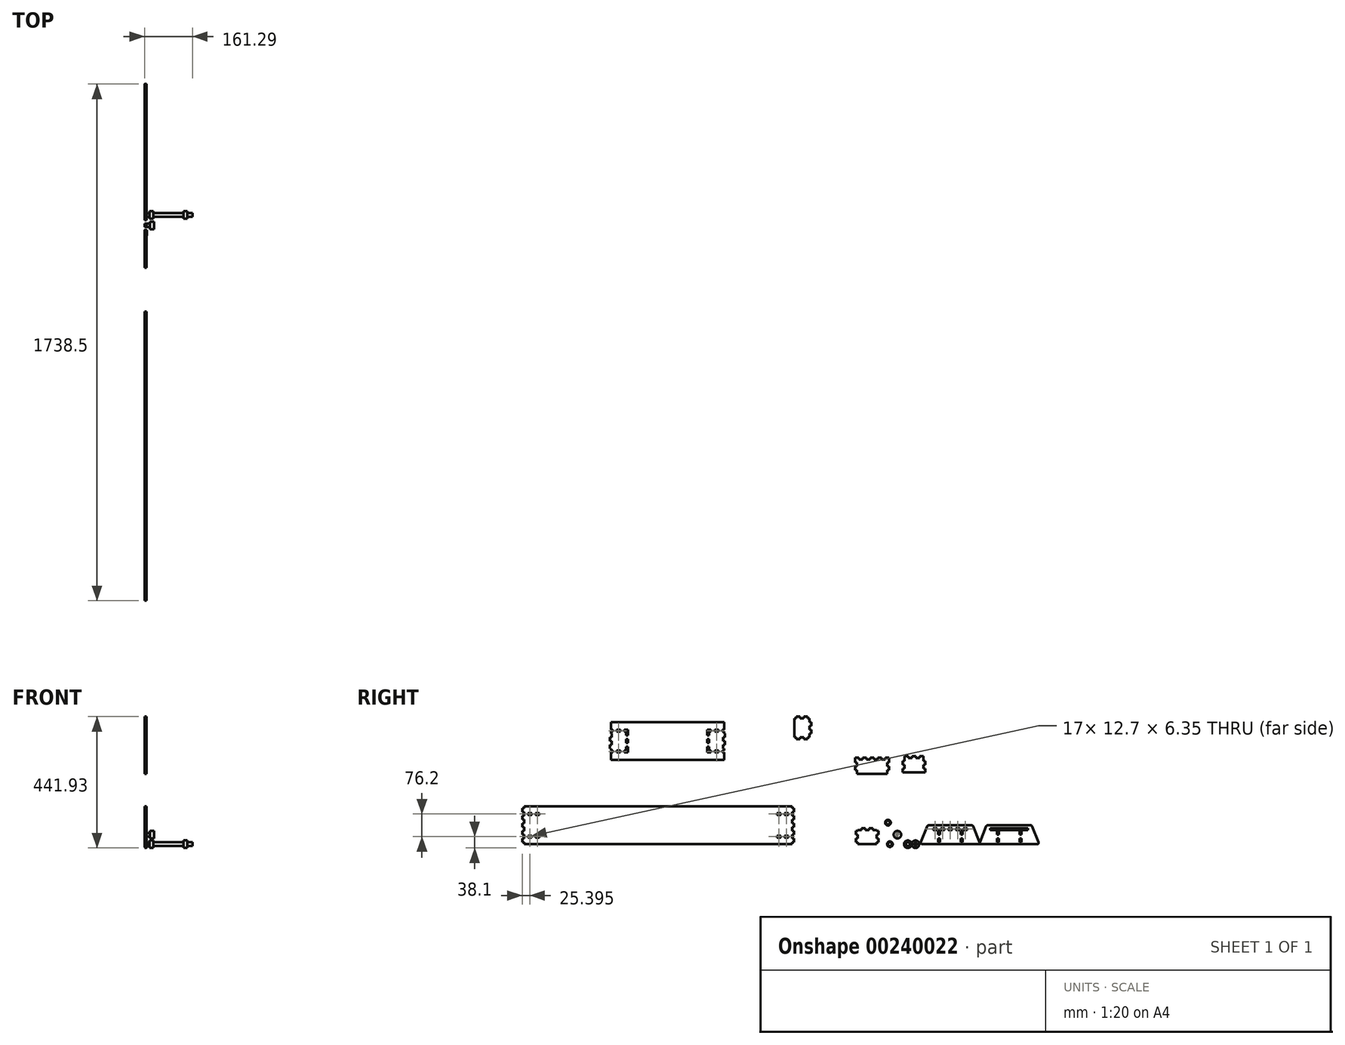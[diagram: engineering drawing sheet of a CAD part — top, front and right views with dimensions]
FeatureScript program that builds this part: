
annotation { "Feature Type Name" : "Feature", "Feature Type Description" : "" }
export const myFeature = defineFeature(function(context is Context, id is Id, definition is map)
    precondition{}
    {
        {
            var Q0;
            Q0=qCreatedBy(makeId("Right.planeOp"),FACE);
            var sketch = newSketch(context, id + "F0", { "sketchPlane" : qUnion([Q0])});
            skLineSegment(sketch, "E0.bottom", {"start": v(0, 0) * mm, "end": v(152.4, 0) * mm});
            skLineSegment(sketch, "E0.top", {"start": v(0, 101.6) * mm, "end": v(152.4, 101.6) * mm});
            skLineSegment(sketch, "E0.left", {"start": v(0, 0) * mm, "end": v(0, 101.6) * mm});
            skLineSegment(sketch, "E0.right", {"start": v(152.4, 0) * mm, "end": v(152.4, 101.6) * mm});
            skLineSegment(sketch, "E1", {"start": v(76.2, 101.6) * mm, "end": v(76.2, 0) * mm, "construction": true});
            skLineSegment(sketch, "E2", {"start": v(0, 50.8) * mm, "end": v(152.4, 50.8) * mm, "construction": true});
            skLineSegment(sketch, "E3", {"start": v(76.2, 53.98) * mm, "end": v(82.55, 53.98) * mm});
            skLineSegment(sketch, "E4", {"start": v(82.55, 53.98) * mm, "end": v(82.55, 50.8) * mm});
            skLineSegment(sketch, "E5.MirrorCS", {"start": v(69.85, 53.98) * mm, "end": v(69.85, 50.8) * mm});
            skLineSegment(sketch, "E6.MirrorCS", {"start": v(76.2, 53.98) * mm, "end": v(69.85, 53.98) * mm});
            skLineSegment(sketch, "E7.MirrorCS", {"start": v(82.55, 47.63) * mm, "end": v(82.55, 50.8) * mm});
            skLineSegment(sketch, "E8.MirrorCS", {"start": v(76.2, 47.63) * mm, "end": v(82.55, 47.63) * mm});
            skLineSegment(sketch, "E9.MirrorCS", {"start": v(76.2, 47.63) * mm, "end": v(69.85, 47.63) * mm});
            skLineSegment(sketch, "E10.MirrorCS", {"start": v(69.85, 47.63) * mm, "end": v(69.85, 50.8) * mm});
            skLineSegment(sketch, "E11.1.0.0", {"start": v(101.6, 53.98) * mm, "end": v(107.95, 53.98) * mm});
            skLineSegment(sketch, "E11.1.0.1", {"start": v(101.6, 53.98) * mm, "end": v(95.25, 53.98) * mm});
            skLineSegment(sketch, "E11.1.0.2", {"start": v(95.25, 53.98) * mm, "end": v(95.25, 50.8) * mm});
            skLineSegment(sketch, "E11.1.0.3", {"start": v(95.25, 47.63) * mm, "end": v(95.25, 50.8) * mm});
            skLineSegment(sketch, "E11.1.0.4", {"start": v(101.6, 47.63) * mm, "end": v(95.25, 47.63) * mm});
            skLineSegment(sketch, "E11.1.0.5", {"start": v(101.6, 47.63) * mm, "end": v(107.95, 47.63) * mm});
            skLineSegment(sketch, "E11.1.0.6", {"start": v(107.95, 47.63) * mm, "end": v(107.95, 50.8) * mm});
            skLineSegment(sketch, "E11.1.0.7", {"start": v(107.95, 53.98) * mm, "end": v(107.95, 50.8) * mm});
            skLineSegment(sketch, "E11.2.0.0", {"start": v(127, 53.98) * mm, "end": v(133.35, 53.98) * mm});
            skLineSegment(sketch, "E11.2.0.1", {"start": v(127, 53.98) * mm, "end": v(120.65, 53.98) * mm});
            skLineSegment(sketch, "E11.2.0.2", {"start": v(120.65, 53.98) * mm, "end": v(120.65, 50.8) * mm});
            skLineSegment(sketch, "E11.2.0.3", {"start": v(120.65, 47.63) * mm, "end": v(120.65, 50.8) * mm});
            skLineSegment(sketch, "E11.2.0.4", {"start": v(127, 47.63) * mm, "end": v(120.65, 47.63) * mm});
            skLineSegment(sketch, "E11.2.0.5", {"start": v(127, 47.63) * mm, "end": v(133.35, 47.63) * mm});
            skLineSegment(sketch, "E11.2.0.6", {"start": v(133.35, 47.63) * mm, "end": v(133.35, 50.8) * mm});
            skLineSegment(sketch, "E11.2.0.7", {"start": v(133.35, 53.98) * mm, "end": v(133.35, 50.8) * mm});
            skLineSegment(sketch, "E11.direction1", {"start": v(76.2, 53.98) * mm, "end": v(101.6, 53.98) * mm, "construction": true});
            skLineSegment(sketch, "E11.direction2", {"start": v(76.2, 53.98) * mm, "end": v(25.4, 53.98) * mm, "construction": true});
            skLineSegment(sketch, "E12.0.0.1", {"start": v(25.4, 53.97) * mm, "end": v(31.75, 53.98) * mm});
            skLineSegment(sketch, "E12.3.0.1", {"start": v(25.4, 53.97) * mm, "end": v(19.05, 53.97) * mm});
            skLineSegment(sketch, "E12.6.0.1", {"start": v(19.05, 53.98) * mm, "end": v(19.05, 50.8) * mm});
            skLineSegment(sketch, "E12.9.0.1", {"start": v(19.05, 47.62) * mm, "end": v(19.05, 50.8) * mm});
            skLineSegment(sketch, "E12.12.0.1", {"start": v(25.4, 47.63) * mm, "end": v(19.05, 47.63) * mm});
            skLineSegment(sketch, "E12.15.0.1", {"start": v(25.4, 47.63) * mm, "end": v(31.75, 47.63) * mm});
            skLineSegment(sketch, "E12.18.0.1", {"start": v(31.75, 47.62) * mm, "end": v(31.75, 50.8) * mm});
            skLineSegment(sketch, "E12.21.0.1", {"start": v(31.75, 53.98) * mm, "end": v(31.75, 50.8) * mm});
            skLineSegment(sketch, "E12.0.1.1", {"start": v(50.8, 53.97) * mm, "end": v(57.15, 53.98) * mm});
            skLineSegment(sketch, "E12.3.1.1", {"start": v(50.8, 53.97) * mm, "end": v(44.45, 53.97) * mm});
            skLineSegment(sketch, "E12.6.1.1", {"start": v(44.45, 53.98) * mm, "end": v(44.45, 50.8) * mm});
            skLineSegment(sketch, "E12.9.1.1", {"start": v(44.45, 47.62) * mm, "end": v(44.45, 50.8) * mm});
            skLineSegment(sketch, "E12.12.1.1", {"start": v(50.8, 47.63) * mm, "end": v(44.45, 47.63) * mm});
            skLineSegment(sketch, "E12.15.1.1", {"start": v(50.8, 47.63) * mm, "end": v(57.15, 47.63) * mm});
            skLineSegment(sketch, "E12.18.1.1", {"start": v(57.15, 47.62) * mm, "end": v(57.15, 50.8) * mm});
            skLineSegment(sketch, "E12.21.1.1", {"start": v(57.15, 53.98) * mm, "end": v(57.15, 50.8) * mm});
            skLineSegment(sketch, "E13.bottom", {"start": v(34.93, 44.45) * mm, "end": v(41.28, 44.45) * mm});
            skLineSegment(sketch, "E13.top", {"start": v(34.93, 31.75) * mm, "end": v(41.28, 31.75) * mm});
            skLineSegment(sketch, "E13.left", {"start": v(34.93, 44.45) * mm, "end": v(34.93, 31.75) * mm});
            skLineSegment(sketch, "E13.right", {"start": v(41.28, 44.45) * mm, "end": v(41.28, 31.75) * mm});
            skLineSegment(sketch, "E14.0.1.0", {"start": v(41.28, 19.05) * mm, "end": v(41.28, 6.35) * mm});
            skLineSegment(sketch, "E14.0.1.1", {"start": v(34.93, 19.05) * mm, "end": v(41.28, 19.05) * mm});
            skLineSegment(sketch, "E14.0.1.2", {"start": v(34.93, 19.05) * mm, "end": v(34.93, 6.35) * mm});
            skLineSegment(sketch, "E14.0.1.3", {"start": v(34.93, 6.35) * mm, "end": v(41.28, 6.35) * mm});
            skLineSegment(sketch, "E14.direction1", {"start": v(41.28, 31.75) * mm, "end": v(53.98, 31.75) * mm, "construction": true});
            skLineSegment(sketch, "E14.direction2", {"start": v(41.28, 31.75) * mm, "end": v(41.28, 6.35) * mm, "construction": true});
            skLineSegment(sketch, "E15.MirrorCS", {"start": v(111.12, 44.45) * mm, "end": v(111.12, 31.75) * mm});
            skLineSegment(sketch, "E16.MirrorCS", {"start": v(117.47, 44.45) * mm, "end": v(111.12, 44.45) * mm});
            skLineSegment(sketch, "E17.MirrorCS", {"start": v(117.47, 44.45) * mm, "end": v(117.47, 31.75) * mm});
            skLineSegment(sketch, "E18.MirrorCS", {"start": v(117.47, 31.75) * mm, "end": v(111.12, 31.75) * mm});
            skLineSegment(sketch, "E19.MirrorCS", {"start": v(117.47, 19.05) * mm, "end": v(111.12, 19.05) * mm});
            skLineSegment(sketch, "E20.MirrorCS", {"start": v(117.47, 19.05) * mm, "end": v(117.47, 6.35) * mm});
            skLineSegment(sketch, "E21.MirrorCS", {"start": v(117.47, 6.35) * mm, "end": v(111.12, 6.35) * mm});
            skLineSegment(sketch, "E22.MirrorCS", {"start": v(111.12, 31.75) * mm, "end": v(111.12, 6.35) * mm, "construction": true});
            skLineSegment(sketch, "E23", {"start": v(111.12, 19.05) * mm, "end": v(111.12, 6.35) * mm});
            skSolve(sketch);
        }
        {
            var Q0;
            Q0=makeQuery(id+"F0.imprint","IMPRINT",FACE,{"disambiguationData":[TD([[makeQuery(id+"F0.imprint","IMPRINT",EDGE,{"derivedFrom":sQuery(id+"F0.wireOp",EDGE,"E0.bottom")}),1.0]])]});
            extrude(context, id + "F1", {"entities" : qUnion([Q0]), "depth" : 6.35 * mm});
        }
        {
            var Q0;
            Q0=qCreatedBy(makeId("Right.planeOp"),FACE);
            var sketch = newSketch(context, id + "F2", { "sketchPlane" : qUnion([Q0])});
            skLineSegment(sketch, "E24.bottom", {"start": v(198.38, 0) * mm, "end": v(350.78, 0) * mm});
            skLineSegment(sketch, "E24.top", {"start": v(198.38, 101.6) * mm, "end": v(350.78, 101.6) * mm});
            skLineSegment(sketch, "E24.left", {"start": v(198.38, 0) * mm, "end": v(198.38, 101.6) * mm});
            skLineSegment(sketch, "E24.right", {"start": v(350.78, 0) * mm, "end": v(350.78, 101.6) * mm});
            skLineSegment(sketch, "E25", {"start": v(198.38, 50.8) * mm, "end": v(350.78, 50.8) * mm, "construction": true});
            skLineSegment(sketch, "E26.bottom", {"start": v(211.08, 53.98) * mm, "end": v(338.08, 53.98) * mm});
            skLineSegment(sketch, "E26.top", {"start": v(211.08, 47.63) * mm, "end": v(338.08, 47.63) * mm});
            skLineSegment(sketch, "E26.left", {"start": v(211.08, 53.98) * mm, "end": v(211.08, 47.63) * mm});
            skLineSegment(sketch, "E26.right", {"start": v(338.08, 53.98) * mm, "end": v(338.08, 47.63) * mm});
            skLineSegment(sketch, "E27.bottom", {"start": v(233.3, 44.45) * mm, "end": v(239.66, 44.45) * mm});
            skLineSegment(sketch, "E27.top", {"start": v(233.3, 31.75) * mm, "end": v(239.66, 31.75) * mm});
            skLineSegment(sketch, "E27.left", {"start": v(233.3, 44.45) * mm, "end": v(233.3, 31.75) * mm});
            skLineSegment(sketch, "E27.right", {"start": v(239.66, 44.45) * mm, "end": v(239.66, 31.75) * mm});
            skLineSegment(sketch, "E28.bottom", {"start": v(233.3, 19.05) * mm, "end": v(239.66, 19.05) * mm});
            skLineSegment(sketch, "E28.top", {"start": v(233.3, 6.35) * mm, "end": v(239.66, 6.35) * mm});
            skLineSegment(sketch, "E28.left", {"start": v(233.3, 19.05) * mm, "end": v(233.3, 6.35) * mm});
            skLineSegment(sketch, "E28.right", {"start": v(239.66, 19.05) * mm, "end": v(239.66, 6.35) * mm});
            skLineSegment(sketch, "E29", {"start": v(274.58, 101.6) * mm, "end": v(274.58, 0) * mm, "construction": true});
            skLineSegment(sketch, "E30.MirrorCS", {"start": v(315.86, 44.45) * mm, "end": v(309.5, 44.45) * mm});
            skLineSegment(sketch, "E31.MirrorCS", {"start": v(315.86, 31.75) * mm, "end": v(309.5, 31.75) * mm});
            skLineSegment(sketch, "E32.MirrorCS", {"start": v(315.86, 44.45) * mm, "end": v(315.86, 31.75) * mm});
            skLineSegment(sketch, "E33.MirrorCS", {"start": v(315.86, 19.05) * mm, "end": v(315.86, 6.35) * mm});
            skLineSegment(sketch, "E34.MirrorCS", {"start": v(315.86, 6.35) * mm, "end": v(309.5, 6.35) * mm});
            skLineSegment(sketch, "E35.MirrorCS", {"start": v(309.5, 19.05) * mm, "end": v(309.5, 6.35) * mm});
            skLineSegment(sketch, "E36.MirrorCS", {"start": v(309.5, 44.45) * mm, "end": v(309.5, 31.75) * mm});
            skLineSegment(sketch, "E37.MirrorCS", {"start": v(315.86, 19.05) * mm, "end": v(309.5, 19.05) * mm});
            skSolve(sketch);
        }
        {
            var Q0;
            Q0=makeQuery(id+"F2.imprint","IMPRINT",FACE,{"disambiguationData":[TD([[makeQuery(id+"F2.imprint","IMPRINT",EDGE,{"derivedFrom":sQuery(id+"F2.wireOp",EDGE,"E24.bottom")}),1.0]])]});
            extrude(context, id + "F3", {"entities" : qUnion([Q0]), "depth" : 6.35 * mm});
        }
        {
            var Q0;
            Q0=qCreatedBy(makeId("Right.planeOp"),FACE);
            var sketch = newSketch(context, id + "F4", { "sketchPlane" : qUnion([Q0])});
            skLineSegment(sketch, "E38.bottom", {"start": v(-164.83, 0) * mm, "end": v(-241.03, 0) * mm});
            skLineSegment(sketch, "E38.top", {"start": v(-164.83, 53.98) * mm, "end": v(-241.03, 53.98) * mm});
            skLineSegment(sketch, "E38.left", {"start": v(-164.83, 0) * mm, "end": v(-164.83, 53.97) * mm});
            skLineSegment(sketch, "E38.right", {"start": v(-241.03, 0) * mm, "end": v(-241.03, 53.98) * mm});
            skLineSegment(sketch, "E39.bottom", {"start": v(-164.83, 0) * mm, "end": v(-171.18, 0) * mm});
            skLineSegment(sketch, "E39.top", {"start": v(-164.83, 6.35) * mm, "end": v(-171.18, 6.35) * mm});
            skLineSegment(sketch, "E39.left", {"start": v(-164.83, 0) * mm, "end": v(-164.83, 6.35) * mm});
            skLineSegment(sketch, "E39.right", {"start": v(-171.18, 0) * mm, "end": v(-171.18, 6.35) * mm});
            skLineSegment(sketch, "E40.bottom", {"start": v(-164.83, 19.05) * mm, "end": v(-171.18, 19.05) * mm});
            skLineSegment(sketch, "E40.top", {"start": v(-164.83, 31.75) * mm, "end": v(-171.18, 31.75) * mm});
            skLineSegment(sketch, "E40.left", {"start": v(-164.83, 19.05) * mm, "end": v(-164.83, 31.75) * mm});
            skLineSegment(sketch, "E40.right", {"start": v(-171.18, 19.05) * mm, "end": v(-171.18, 31.75) * mm});
            skLineSegment(sketch, "E41.bottom", {"start": v(-164.83, 53.98) * mm, "end": v(-171.18, 53.98) * mm});
            skLineSegment(sketch, "E41.top", {"start": v(-164.83, 47.62) * mm, "end": v(-171.18, 47.62) * mm});
            skLineSegment(sketch, "E41.left", {"start": v(-164.83, 53.98) * mm, "end": v(-164.83, 47.62) * mm});
            skLineSegment(sketch, "E42", {"start": v(-202.93, 53.98) * mm, "end": v(-202.93, 0) * mm, "construction": true});
            skLineSegment(sketch, "E43.MirrorCS", {"start": v(-241.03, 47.62) * mm, "end": v(-234.68, 47.62) * mm});
            skLineSegment(sketch, "E44.MirrorCS", {"start": v(-234.68, 53.98) * mm, "end": v(-234.68, 47.62) * mm});
            skLineSegment(sketch, "E45.MirrorCS", {"start": v(-234.68, 19.05) * mm, "end": v(-234.68, 31.75) * mm});
            skLineSegment(sketch, "E46.MirrorCS", {"start": v(-241.03, 31.75) * mm, "end": v(-234.68, 31.75) * mm});
            skLineSegment(sketch, "E47.MirrorCS", {"start": v(-241.03, 19.05) * mm, "end": v(-234.68, 19.05) * mm});
            skLineSegment(sketch, "E48.MirrorCS", {"start": v(-234.68, 0) * mm, "end": v(-234.68, 6.35) * mm});
            skLineSegment(sketch, "E49.MirrorCS", {"start": v(-241.03, 6.35) * mm, "end": v(-234.68, 6.35) * mm});
            skLineSegment(sketch, "E50.bottom", {"start": v(-183.88, 53.98) * mm, "end": v(-196.58, 53.98) * mm});
            skLineSegment(sketch, "E51.bottom", {"start": v(-171.18, 53.98) * mm, "end": v(-183.88, 53.98) * mm});
            skLineSegment(sketch, "E51.top", {"start": v(-171.18, 47.62) * mm, "end": v(-183.88, 47.62) * mm});
            skLineSegment(sketch, "E51.left", {"start": v(-171.18, 53.98) * mm, "end": v(-171.18, 47.62) * mm});
            skLineSegment(sketch, "E51.right", {"start": v(-183.88, 53.98) * mm, "end": v(-183.88, 47.62) * mm});
            skLineSegment(sketch, "E52.MirrorCS", {"start": v(-234.68, 47.62) * mm, "end": v(-221.98, 47.62) * mm});
            skLineSegment(sketch, "E53.MirrorCS", {"start": v(-221.98, 53.98) * mm, "end": v(-221.98, 47.62) * mm});
            skLineSegment(sketch, "E54.bottom", {"start": v(-196.58, 53.98) * mm, "end": v(-202.93, 53.98) * mm});
            skLineSegment(sketch, "E54.top", {"start": v(-196.58, 47.62) * mm, "end": v(-202.93, 47.62) * mm});
            skLineSegment(sketch, "E54.left", {"start": v(-196.58, 53.98) * mm, "end": v(-196.58, 47.62) * mm});
            skLineSegment(sketch, "E54.right", {"start": v(-202.93, 53.98) * mm, "end": v(-202.93, 47.62) * mm});
            skLineSegment(sketch, "E55.MirrorCS", {"start": v(-209.28, 47.62) * mm, "end": v(-202.93, 47.62) * mm});
            skLineSegment(sketch, "E56.MirrorCS", {"start": v(-209.28, 53.98) * mm, "end": v(-209.28, 47.62) * mm});
            skLineSegment(sketch, "E57.top", {"start": v(-164.83, 44.45) * mm, "end": v(-171.18, 44.45) * mm});
            skLineSegment(sketch, "E57.left", {"start": v(-164.83, 47.62) * mm, "end": v(-164.83, 44.45) * mm});
            skLineSegment(sketch, "E57.right", {"start": v(-171.18, 47.62) * mm, "end": v(-171.18, 44.45) * mm});
            skLineSegment(sketch, "E58.MirrorCS", {"start": v(-234.68, 47.62) * mm, "end": v(-234.68, 44.45) * mm});
            skLineSegment(sketch, "E59.MirrorCS", {"start": v(-241.03, 44.45) * mm, "end": v(-234.68, 44.45) * mm});
            skSolve(sketch);
        }
        {
            var Q0;
            {var subQ4=sQuery(id+"F4.wireOp",EDGE,"E39.top");Q0=makeQuery(id+"F4.imprint","IMPRINT",FACE,{"disambiguationData":[TD([[makeQuery(id+"F4.imprint","IMPRINT",EDGE,{"derivedFrom":subQ4}),-1.0]])]});}
            extrude(context, id + "F5", {"entities" : qUnion([Q0]), "depth" : 6.35 * mm});
        }
        {
            var Q0;
            Q0=qCreatedBy(makeId("Right.planeOp"),FACE);
            var sketch = newSketch(context, id + "F6", { "sketchPlane" : qUnion([Q0])});
            skLineSegment(sketch, "E60.bottom", {"start": v(-450.34, 0) * mm, "end": v(-1364.74, 0) * mm});
            skLineSegment(sketch, "E60.top", {"start": v(-450.34, 127) * mm, "end": v(-1364.74, 127) * mm});
            skLineSegment(sketch, "E60.left", {"start": v(-450.34, 0) * mm, "end": v(-450.34, 127) * mm});
            skLineSegment(sketch, "E60.right", {"start": v(-1364.74, 0) * mm, "end": v(-1364.74, 127) * mm});
            skLineSegment(sketch, "E61.bottom", {"start": v(-450.34, 127) * mm, "end": v(-456.7, 127) * mm});
            skLineSegment(sketch, "E61.top", {"start": v(-450.34, 120.65) * mm, "end": v(-456.7, 120.65) * mm});
            skLineSegment(sketch, "E61.left", {"start": v(-450.34, 127) * mm, "end": v(-450.34, 120.65) * mm});
            skLineSegment(sketch, "E61.right", {"start": v(-456.7, 127) * mm, "end": v(-456.7, 120.65) * mm});
            skLineSegment(sketch, "E62.bottom", {"start": v(-450.34, 107.95) * mm, "end": v(-456.7, 107.95) * mm});
            skLineSegment(sketch, "E62.top", {"start": v(-450.34, 95.25) * mm, "end": v(-456.7, 95.25) * mm});
            skLineSegment(sketch, "E62.left", {"start": v(-450.34, 107.95) * mm, "end": v(-450.34, 95.25) * mm});
            skLineSegment(sketch, "E62.right", {"start": v(-456.7, 107.95) * mm, "end": v(-456.7, 95.25) * mm});
            skLineSegment(sketch, "E63.0.1.0", {"start": v(-456.7, 82.55) * mm, "end": v(-456.7, 69.85) * mm});
            skLineSegment(sketch, "E63.0.1.1", {"start": v(-450.34, 69.85) * mm, "end": v(-456.7, 69.85) * mm});
            skLineSegment(sketch, "E63.0.1.2", {"start": v(-450.34, 82.55) * mm, "end": v(-456.7, 82.55) * mm});
            skLineSegment(sketch, "E63.0.2.0", {"start": v(-456.7, 57.15) * mm, "end": v(-456.7, 44.45) * mm});
            skLineSegment(sketch, "E63.0.2.1", {"start": v(-450.34, 44.45) * mm, "end": v(-456.7, 44.45) * mm});
            skLineSegment(sketch, "E63.0.2.2", {"start": v(-450.34, 57.15) * mm, "end": v(-456.7, 57.15) * mm});
            skLineSegment(sketch, "E63.0.3.0", {"start": v(-456.7, 31.75) * mm, "end": v(-456.7, 19.05) * mm});
            skLineSegment(sketch, "E63.0.3.1", {"start": v(-450.34, 19.05) * mm, "end": v(-456.7, 19.05) * mm});
            skLineSegment(sketch, "E63.0.3.2", {"start": v(-450.34, 31.75) * mm, "end": v(-456.7, 31.75) * mm});
            skLineSegment(sketch, "E63.direction1", {"start": v(-456.7, 95.25) * mm, "end": v(-431.3, 95.25) * mm, "construction": true});
            skLineSegment(sketch, "E63.direction2", {"start": v(-456.7, 95.25) * mm, "end": v(-456.7, 69.85) * mm, "construction": true});
            skLineSegment(sketch, "E64", {"start": v(-450.34, 63.5) * mm, "end": v(-1364.74, 63.5) * mm, "construction": true});
            skLineSegment(sketch, "E65.MirrorCS", {"start": v(-450.34, 6.35) * mm, "end": v(-456.7, 6.35) * mm});
            skLineSegment(sketch, "E66.MirrorCS", {"start": v(-456.7, 0) * mm, "end": v(-456.7, 6.35) * mm});
            skLineSegment(sketch, "E67.left", {"start": v(-456.7, 104.78) * mm, "end": v(-456.7, 98.43) * mm});
            skLineSegment(sketch, "E68.direction1", {"start": v(-456.7, 69.85) * mm, "end": v(-482.1, 69.85) * mm, "construction": true});
            skLineSegment(sketch, "E69.MirrorCS", {"start": v(-456.7, 31.75) * mm, "end": v(-456.7, 57.15) * mm, "construction": true});
            skLineSegment(sketch, "E70", {"start": v(-907.54, 0) * mm, "end": v(-907.54, 127) * mm, "construction": true});
            skLineSegment(sketch, "E71.MirrorCS", {"start": v(-1364.74, 127) * mm, "end": v(-1358.4, 127) * mm});
            skLineSegment(sketch, "E72.MirrorCS", {"start": v(-1358.4, 104.77) * mm, "end": v(-1358.4, 98.42) * mm});
            skLineSegment(sketch, "E73.MirrorCS", {"start": v(-1358.4, 82.55) * mm, "end": v(-1358.4, 69.85) * mm});
            skLineSegment(sketch, "E74.MirrorCS", {"start": v(-1364.74, 95.25) * mm, "end": v(-1358.4, 95.25) * mm});
            skLineSegment(sketch, "E75.MirrorCS", {"start": v(-1364.74, 107.95) * mm, "end": v(-1358.4, 107.95) * mm});
            skLineSegment(sketch, "E76.MirrorCS", {"start": v(-1364.74, 120.65) * mm, "end": v(-1358.4, 120.65) * mm});
            skLineSegment(sketch, "E77.MirrorCS", {"start": v(-1358.4, 127) * mm, "end": v(-1358.4, 120.65) * mm});
            skLineSegment(sketch, "E78.MirrorCS", {"start": v(-1364.74, 127) * mm, "end": v(-1364.74, 120.65) * mm});
            skLineSegment(sketch, "E79.MirrorCS", {"start": v(-1364.74, 19.05) * mm, "end": v(-1358.4, 19.05) * mm});
            skLineSegment(sketch, "E80.MirrorCS", {"start": v(-1364.74, 44.45) * mm, "end": v(-1358.4, 44.45) * mm});
            skLineSegment(sketch, "E81.MirrorCS", {"start": v(-1358.4, 107.95) * mm, "end": v(-1358.4, 95.25) * mm});
            skLineSegment(sketch, "E82.MirrorCS", {"start": v(-1364.74, 31.75) * mm, "end": v(-1358.4, 31.75) * mm});
            skLineSegment(sketch, "E83.MirrorCS", {"start": v(-1364.74, 57.15) * mm, "end": v(-1358.4, 57.15) * mm});
            skLineSegment(sketch, "E84.MirrorCS", {"start": v(-1364.74, 6.35) * mm, "end": v(-1358.4, 6.35) * mm});
            skLineSegment(sketch, "E85.MirrorCS", {"start": v(-1364.74, 82.55) * mm, "end": v(-1358.4, 82.55) * mm});
            skLineSegment(sketch, "E86.MirrorCS", {"start": v(-1364.74, 69.85) * mm, "end": v(-1358.4, 69.85) * mm});
            skLineSegment(sketch, "E87.MirrorCS", {"start": v(-1358.4, 95.25) * mm, "end": v(-1358.4, 69.85) * mm, "construction": true});
            skLineSegment(sketch, "E88.MirrorCS", {"start": v(-1358.4, 0) * mm, "end": v(-1358.4, 6.35) * mm});
            skLineSegment(sketch, "E89.MirrorCS", {"start": v(-1358.4, 57.15) * mm, "end": v(-1358.4, 44.45) * mm});
            skLineSegment(sketch, "E90.MirrorCS", {"start": v(-1358.4, 69.85) * mm, "end": v(-1333, 69.85) * mm, "construction": true});
            skLineSegment(sketch, "E91.MirrorCS", {"start": v(-1364.74, 107.95) * mm, "end": v(-1364.74, 95.25) * mm});
            skLineSegment(sketch, "E92.MirrorCS", {"start": v(-1358.4, 31.75) * mm, "end": v(-1358.4, 19.05) * mm});
            skLineSegment(sketch, "E93.MirrorCS", {"start": v(-1364.74, 63.5) * mm, "end": v(-450.34, 63.5) * mm, "construction": true});
            skLineSegment(sketch, "E94.MirrorCS", {"start": v(-1358.4, 31.75) * mm, "end": v(-1358.4, 57.15) * mm, "construction": true});
            skLineSegment(sketch, "E95.MirrorCS", {"start": v(-1358.4, 95.25) * mm, "end": v(-1383.8, 95.25) * mm, "construction": true});
            skLineSegment(sketch, "E96.MirrorCS", {"start": v(-1364.74, 127) * mm, "end": v(-450.34, 127) * mm});
            skLineSegment(sketch, "E97.MirrorCS", {"start": v(-1364.74, 0) * mm, "end": v(-450.34, 0) * mm});
            skLineSegment(sketch, "E98", {"start": v(-456.7, 28.58) * mm, "end": v(-456.7, 22.23) * mm});
            skLineSegment(sketch, "E99", {"start": v(-1358.4, 28.57) * mm, "end": v(-1358.4, 22.22) * mm});
            skLineSegment(sketch, "E100.bottom", {"start": v(-469.4, 104.78) * mm, "end": v(-482.1, 104.78) * mm});
            skLineSegment(sketch, "E100.top", {"start": v(-469.4, 98.43) * mm, "end": v(-482.1, 98.43) * mm});
            skLineSegment(sketch, "E100.left", {"start": v(-469.4, 104.78) * mm, "end": v(-469.4, 98.43) * mm});
            skLineSegment(sketch, "E100.right", {"start": v(-482.1, 104.78) * mm, "end": v(-482.1, 98.43) * mm});
            skLineSegment(sketch, "E101.1.0.0", {"start": v(-494.8, 104.78) * mm, "end": v(-494.8, 98.43) * mm});
            skLineSegment(sketch, "E101.1.0.1", {"start": v(-507.5, 104.78) * mm, "end": v(-507.5, 98.43) * mm});
            skLineSegment(sketch, "E101.1.0.2", {"start": v(-494.8, 98.43) * mm, "end": v(-507.5, 98.43) * mm});
            skLineSegment(sketch, "E101.1.0.3", {"start": v(-494.8, 104.78) * mm, "end": v(-507.5, 104.78) * mm});
            skLineSegment(sketch, "E101.direction1", {"start": v(-482.1, 98.43) * mm, "end": v(-507.5, 98.43) * mm, "construction": true});
            skLineSegment(sketch, "E102.MirrorCS", {"start": v(-494.8, 28.57) * mm, "end": v(-507.5, 28.57) * mm});
            skLineSegment(sketch, "E103.MirrorCS", {"start": v(-507.5, 22.23) * mm, "end": v(-507.5, 28.58) * mm});
            skLineSegment(sketch, "E104.MirrorCS", {"start": v(-482.1, 28.57) * mm, "end": v(-507.5, 28.57) * mm, "construction": true});
            skLineSegment(sketch, "E105.MirrorCS", {"start": v(-482.1, 22.23) * mm, "end": v(-482.1, 28.58) * mm});
            skLineSegment(sketch, "E106.MirrorCS", {"start": v(-469.4, 22.23) * mm, "end": v(-469.4, 28.58) * mm});
            skLineSegment(sketch, "E107.MirrorCS", {"start": v(-469.4, 28.57) * mm, "end": v(-482.1, 28.57) * mm});
            skLineSegment(sketch, "E108.MirrorCS", {"start": v(-469.4, 22.22) * mm, "end": v(-482.1, 22.22) * mm});
            skLineSegment(sketch, "E109.MirrorCS", {"start": v(-494.8, 22.23) * mm, "end": v(-494.8, 28.58) * mm});
            skLineSegment(sketch, "E110.MirrorCS", {"start": v(-494.8, 22.22) * mm, "end": v(-507.5, 22.22) * mm});
            skLineSegment(sketch, "E111.MirrorCS", {"start": v(-1307.6, 104.77) * mm, "end": v(-1307.6, 98.42) * mm});
            skLineSegment(sketch, "E112.MirrorCS", {"start": v(-1320.3, 22.22) * mm, "end": v(-1320.3, 28.57) * mm});
            skLineSegment(sketch, "E113.MirrorCS", {"start": v(-1333, 22.22) * mm, "end": v(-1333, 28.57) * mm});
            skLineSegment(sketch, "E114.MirrorCS", {"start": v(-1307.6, 22.22) * mm, "end": v(-1307.6, 28.57) * mm});
            skLineSegment(sketch, "E115.MirrorCS", {"start": v(-1345.7, 104.77) * mm, "end": v(-1345.7, 98.42) * mm});
            skLineSegment(sketch, "E116.MirrorCS", {"start": v(-1333, 104.77) * mm, "end": v(-1333, 98.42) * mm});
            skLineSegment(sketch, "E117.MirrorCS", {"start": v(-1345.7, 22.22) * mm, "end": v(-1345.7, 28.57) * mm});
            skLineSegment(sketch, "E118.MirrorCS", {"start": v(-1320.3, 104.77) * mm, "end": v(-1320.3, 98.42) * mm});
            skLineSegment(sketch, "E119.MirrorCS", {"start": v(-1320.3, 28.57) * mm, "end": v(-1307.6, 28.57) * mm});
            skLineSegment(sketch, "E120.MirrorCS", {"start": v(-1345.7, 98.43) * mm, "end": v(-1333, 98.43) * mm});
            skLineSegment(sketch, "E121.MirrorCS", {"start": v(-1345.7, 104.78) * mm, "end": v(-1333, 104.78) * mm});
            skLineSegment(sketch, "E122.MirrorCS", {"start": v(-1320.3, 104.78) * mm, "end": v(-1307.6, 104.78) * mm});
            skLineSegment(sketch, "E123.MirrorCS", {"start": v(-1320.3, 98.43) * mm, "end": v(-1307.6, 98.43) * mm});
            skLineSegment(sketch, "E124.MirrorCS", {"start": v(-1333, 28.57) * mm, "end": v(-1307.6, 28.57) * mm, "construction": true});
            skLineSegment(sketch, "E125.MirrorCS", {"start": v(-1345.7, 28.57) * mm, "end": v(-1333, 28.57) * mm});
            skLineSegment(sketch, "E126.MirrorCS", {"start": v(-1320.3, 22.22) * mm, "end": v(-1307.6, 22.22) * mm});
            skLineSegment(sketch, "E127.MirrorCS", {"start": v(-1345.7, 22.22) * mm, "end": v(-1333, 22.22) * mm});
            skLineSegment(sketch, "E128.MirrorCS", {"start": v(-1333, 98.43) * mm, "end": v(-1307.6, 98.43) * mm, "construction": true});
            skSolve(sketch);
        }
        {
            var Q0;
            {var subQ4=sQuery(id+"F6.wireOp",EDGE,"E61.top");Q0=makeQuery(id+"F6.imprint","IMPRINT",FACE,{"disambiguationData":[TD([[makeQuery(id+"F6.imprint","IMPRINT",EDGE,{"derivedFrom":subQ4}),1.0]])]});}
            extrude(context, id + "F7", {"entities" : qUnion([Q0]), "depth" : 6.35 * mm});
        }
        {
            var Q0;
            Q0=qCreatedBy(makeId("Right.planeOp"),FACE);
            var sketch = newSketch(context, id + "F8", { "sketchPlane" : qUnion([Q0])});
            skCircle(sketch, "E129", {"center": v(-101.6, 32.09) * mm, "radius": 5.72 * mm});
            skSolve(sketch);
        }
        {
            var Q0;
            Q0=makeQuery(id+"F8.imprint","IMPRINT",FACE,{"disambiguationData":[TD([[makeQuery(id+"F8.imprint","IMPRINT",EDGE,{"derivedFrom":sQuery(id+"F8.wireOp",EDGE,"E129")}),1.0]])]});
            extrude(context, id + "F9", {"entities" : qUnion([Q0]), "depth" : 19.05 * mm});
        }
        {
            var Q0;
            Q0=qCreatedBy(makeId("Right.planeOp"),FACE);
            var sketch = newSketch(context, id + "F10", { "sketchPlane" : qUnion([Q0])});
            skCircle(sketch, "E130", {"center": v(-66.73, 0) * mm, "radius": 5.72 * mm});
            skSolve(sketch);
        }
        {
            var Q0;
            Q0=makeQuery(id+"F10.imprint","IMPRINT",FACE,{"disambiguationData":[TD([[makeQuery(id+"F10.imprint","IMPRINT",EDGE,{"derivedFrom":sQuery(id+"F10.wireOp",EDGE,"E130")}),1.0]])]});
            extrude(context, id + "F11", {"entities" : qUnion([Q0]), "depth" : 17.14 * mm});
        }
        {
            var Q0;
            Q0=makeQuery(id+"F11.opExtrude","CAP_FACE",FACE,{"disambiguationData":[OSD([sQuery(id+"F10.wireOp",EDGE,"E130")])],"isStart":false});
            var sketch = newSketch(context, id + "F12", { "sketchPlane" : qUnion([Q0])});
            skCircle(sketch, "E131", {"center": v(-66.73, 0) * mm, "radius": 12.7 * mm});
            skSolve(sketch);
        }
        {
            var Q0;
            Q0=makeQuery(id+"F12.imprint","IMPRINT",FACE,{"disambiguationData":[TD([[makeQuery(id+"F12.imprint","IMPRINT",EDGE,{"derivedFrom":sQuery(id+"F12.wireOp",EDGE,"E131")}),1.0]])]});
            var Q1;
            Q1=makeQuery(id+"F12.imprint","IMPRINT",FACE,{"disambiguationData":[TD([[makeQuery(id+"F12.imprint","IMPRINT",EDGE,{"derivedFrom":makeQuery(id+"F11.opExtrude","CAP_EDGE",EDGE,{"disambiguationData":[OSD([sQuery(id+"F10.wireOp",EDGE,"E130")])],"isStart":false})}),1.0]])]});
            extrude(context, id + "F13", {"entities" : qUnion([Q0, Q1]), "operationType" : NewBodyOperationType.ADD, "depth" : 12.7 * mm});
        }
        {
            var Q0;
            Q0=makeQuery(id+"F13.opExtrude","CAP_FACE",FACE,{"disambiguationData":[OSD([sQuery(id+"F12.wireOp",EDGE,"E131")])],"isStart":false});
            var sketch = newSketch(context, id + "F14", { "sketchPlane" : qUnion([Q0])});
            skCircle(sketch, "E132", {"center": v(-66.73, 0) * mm, "radius": 6.35 * mm});
            skSolve(sketch);
        }
        {
            var Q0;
            Q0=makeQuery(id+"F14.imprint","IMPRINT",FACE,{"disambiguationData":[TD([[makeQuery(id+"F14.imprint","IMPRINT",EDGE,{"derivedFrom":sQuery(id+"F14.wireOp",EDGE,"E132")}),1.0]])]});
            extrude(context, id + "F15", {"entities" : qUnion([Q0]), "operationType" : NewBodyOperationType.ADD, "depth" : 101.6 * mm});
        }
        {
            var Q0;
            Q0=makeQuery(id+"F15.opExtrude","CAP_FACE",FACE,{"disambiguationData":[OSD([sQuery(id+"F14.wireOp",EDGE,"E132")])],"isStart":false});
            var sketch = newSketch(context, id + "F16", { "sketchPlane" : qUnion([Q0])});
            skCircle(sketch, "E133", {"center": v(-66.73, 0) * mm, "radius": 12.7 * mm});
            skSolve(sketch);
        }
        {
            var Q0;
            Q0=makeQuery(id+"F16.imprint","IMPRINT",FACE,{"disambiguationData":[TD([[makeQuery(id+"F16.imprint","IMPRINT",EDGE,{"derivedFrom":sQuery(id+"F16.wireOp",EDGE,"E133")}),1.0]])]});
            var Q1;
            Q1=makeQuery(id+"F16.imprint","IMPRINT",FACE,{"disambiguationData":[TD([[makeQuery(id+"F16.imprint","IMPRINT",EDGE,{"derivedFrom":makeQuery(id+"F15.opExtrude","CAP_EDGE",EDGE,{"disambiguationData":[OSD([sQuery(id+"F14.wireOp",EDGE,"E132")])],"isStart":false})}),1.0]])]});
            extrude(context, id + "F17", {"entities" : qUnion([Q0, Q1]), "operationType" : NewBodyOperationType.ADD, "depth" : 12.7 * mm});
        }
        {
            var Q0;
            Q0=makeQuery(id+"F17.opExtrude","CAP_FACE",FACE,{"disambiguationData":[OSD([sQuery(id+"F16.wireOp",EDGE,"E133")])],"isStart":false});
            var sketch = newSketch(context, id + "F18", { "sketchPlane" : qUnion([Q0])});
            skCircle(sketch, "E134", {"center": v(-66.73, 0) * mm, "radius": 6.35 * mm});
            skSolve(sketch);
        }
        {
            var Q0;
            Q0=makeQuery(id+"F18.imprint","IMPRINT",FACE,{"disambiguationData":[TD([[makeQuery(id+"F18.imprint","IMPRINT",EDGE,{"derivedFrom":sQuery(id+"F18.wireOp",EDGE,"E134")}),1.0]])]});
            extrude(context, id + "F19", {"entities" : qUnion([Q0]), "operationType" : NewBodyOperationType.ADD, "depth" : 17.14 * mm});
        }
        {
            var Q0;
            Q0=makeQuery(id+"F9.opExtrude","CAP_FACE",FACE,{"disambiguationData":[OSD([sQuery(id+"F8.wireOp",EDGE,"E129")])],"isStart":false});
            var sketch = newSketch(context, id + "F20", { "sketchPlane" : qUnion([Q0])});
            skCircle(sketch, "E135", {"center": v(-101.6, 32.09) * mm, "radius": 12.7 * mm});
            skSolve(sketch);
        }
        {
            var Q0;
            Q0=makeQuery(id+"F20.imprint","IMPRINT",FACE,{"disambiguationData":[TD([[makeQuery(id+"F20.imprint","IMPRINT",EDGE,{"derivedFrom":sQuery(id+"F20.wireOp",EDGE,"E135")}),1.0]])]});
            var Q1;
            Q1=makeQuery(id+"F20.imprint","IMPRINT",FACE,{"disambiguationData":[TD([[makeQuery(id+"F20.imprint","IMPRINT",EDGE,{"derivedFrom":makeQuery(id+"F9.opExtrude","CAP_EDGE",EDGE,{"disambiguationData":[OSD([sQuery(id+"F8.wireOp",EDGE,"E129")])],"isStart":false})}),1.0]])]});
            extrude(context, id + "F21", {"entities" : qUnion([Q0, Q1]), "operationType" : NewBodyOperationType.ADD, "depth" : 12.7 * mm});
        }
        {
            var Q0;
            Q0=qCreatedBy(makeId("Top.planeOp"),FACE);
            var sketch = newSketch(context, id + "F22", { "sketchPlane" : qUnion([Q0])});
            skCircle(sketch, "E136", {"center": v(4.76, -101.6) * mm, "radius": 1.59 * mm});
            skSolve(sketch);
        }
        {
            var Q0;
            Q0=qSketchRegion(id+"F22",true);
            extrude(context, id + "F23", {"entities" : qUnion([Q0]), "operationType" : NewBodyOperationType.REMOVE, "endBound" : BoundingType.THROUGH_ALL, "depth" : 25.4 * mm});
        }
        {
            var Q0;
            Q0=qCreatedBy(makeId("Right.planeOp"),FACE);
            var sketch = newSketch(context, id + "F24", { "sketchPlane" : qUnion([Q0])});
            skCircle(sketch, "E137", {"center": v(-127, 0) * mm, "radius": 9.53 * mm});
            skSolve(sketch);
        }
        {
            var Q0;
            Q0=makeQuery(id+"F24.imprint","IMPRINT",FACE,{"disambiguationData":[TD([[makeQuery(id+"F24.imprint","IMPRINT",EDGE,{"derivedFrom":sQuery(id+"F24.wireOp",EDGE,"E137")}),1.0]])]});
            extrude(context, id + "F25", {"entities" : qUnion([Q0]), "depth" : 8.47 * mm});
        }
        {
            var Q0;
            Q0=qCreatedBy(makeId("Top.planeOp"),FACE);
            var sketch = newSketch(context, id + "F26", { "sketchPlane" : qUnion([Q0])});
            skCircle(sketch, "E138", {"center": v(4.23, -127) * mm, "radius": 1.59 * mm});
            skSolve(sketch);
        }
        {
            var Q0;
            Q0=qSketchRegion(id+"F26",true);
            extrude(context, id + "F27", {"entities" : qUnion([Q0]), "operationType" : NewBodyOperationType.REMOVE, "endBound" : BoundingType.THROUGH_ALL, "depth" : 25.4 * mm});
        }
        {
            var Q0;
            Q0=makeQuery(id+"F25.opExtrude","CAP_FACE",FACE,{"disambiguationData":[OSD([sQuery(id+"F24.wireOp",EDGE,"E137")])],"isStart":true});
            var sketch = newSketch(context, id + "F28", { "sketchPlane" : qUnion([Q0])});
            skCircle(sketch, "E139", {"center": v(127, 0) * mm, "radius": 6.35 * mm});
            skSolve(sketch);
        }
        {
            var Q0;
            Q0=makeQuery(id+"F28.imprint","IMPRINT",FACE,{"disambiguationData":[TD([[makeQuery(id+"F28.imprint","IMPRINT",EDGE,{"derivedFrom":sQuery(id+"F28.wireOp",EDGE,"E139")}),1.0]])]});
            extrude(context, id + "F29", {"entities" : qUnion([Q0]), "operationType" : NewBodyOperationType.REMOVE, "endBound" : BoundingType.UP_TO_NEXT, "oppositeDirection" : true, "depth" : 25.4 * mm});
        }
        {
            var Q0;
            Q0=qCreatedBy(makeId("Right.planeOp"),FACE);
            var sketch = newSketch(context, id + "F30", { "sketchPlane" : qUnion([Q0])});
            skCircle(sketch, "E140", {"center": v(-133.45, 72.65) * mm, "radius": 9.53 * mm});
            skCircle(sketch, "E141", {"center": v(-133.45, 72.65) * mm, "radius": 6.35 * mm});
            skSolve(sketch);
        }
        {
            var Q0;
            Q0=makeQuery(id+"F30.imprint","IMPRINT",FACE,{"disambiguationData":[TD([[makeQuery(id+"F30.imprint","IMPRINT",EDGE,{"derivedFrom":sQuery(id+"F30.wireOp",EDGE,"E140")}),1.0]])]});
            extrude(context, id + "F31", {"entities" : qUnion([Q0]), "depth" : 2.38 * mm});
        }
        {
            var Q0;
            Q0=makeQuery(id+"F5.opExtrude","SWEPT_BODY",BODY,{"disambiguationData":[OSD([sQuery(id+"F4.wireOp",EDGE,"E38.bottom"),sQuery(id+"F4.wireOp",EDGE,"E38.top"),sQuery(id+"F4.wireOp",EDGE,"E38.left"),sQuery(id+"F4.wireOp",EDGE,"E38.right"),sQuery(id+"F4.wireOp",EDGE,"E39.top"),sQuery(id+"F4.wireOp",EDGE,"E39.right"),sQuery(id+"F4.wireOp",EDGE,"E40.bottom"),sQuery(id+"F4.wireOp",EDGE,"E40.top"),sQuery(id+"F4.wireOp",EDGE,"E40.right"),sQuery(id+"F4.wireOp",EDGE,"E45.MirrorCS"),sQuery(id+"F4.wireOp",EDGE,"E46.MirrorCS"),sQuery(id+"F4.wireOp",EDGE,"E47.MirrorCS"),sQuery(id+"F4.wireOp",EDGE,"E48.MirrorCS"),sQuery(id+"F4.wireOp",EDGE,"E49.MirrorCS"),sQuery(id+"F4.wireOp",EDGE,"E50.bottom"),sQuery(id+"F4.wireOp",EDGE,"E51.top"),sQuery(id+"F4.wireOp",EDGE,"E51.right"),sQuery(id+"F4.wireOp",EDGE,"E52.MirrorCS"),sQuery(id+"F4.wireOp",EDGE,"E53.MirrorCS"),sQuery(id+"F4.wireOp",EDGE,"E54.top"),sQuery(id+"F4.wireOp",EDGE,"E54.left"),sQuery(id+"F4.wireOp",EDGE,"E55.MirrorCS"),sQuery(id+"F4.wireOp",EDGE,"E56.MirrorCS"),sQuery(id+"F4.wireOp",EDGE,"E57.top"),sQuery(id+"F4.wireOp",EDGE,"E57.right"),sQuery(id+"F4.wireOp",EDGE,"E58.MirrorCS"),sQuery(id+"F4.wireOp",EDGE,"E59.MirrorCS")])]});
            transform(context, id + "F32", {"entities" : qUnion([Q0]), "transformType" : TransformType.TRANSLATION_3D, "dx" : 0 * mm, "dy" : 0 * mm, "dz" : 0 * mm, "makeCopy" : true});
        }
        {
            var Q0;
            Q0=makeQuery(id+"F32.opPattern","COPY",BODY,{"derivedFrom":makeQuery(id+"F5.opExtrude","SWEPT_BODY",BODY,{"disambiguationData":[OSD([sQuery(id+"F4.wireOp",EDGE,"E38.bottom"),sQuery(id+"F4.wireOp",EDGE,"E38.top"),sQuery(id+"F4.wireOp",EDGE,"E38.left"),sQuery(id+"F4.wireOp",EDGE,"E38.right"),sQuery(id+"F4.wireOp",EDGE,"E39.top"),sQuery(id+"F4.wireOp",EDGE,"E39.right"),sQuery(id+"F4.wireOp",EDGE,"E40.bottom"),sQuery(id+"F4.wireOp",EDGE,"E40.top"),sQuery(id+"F4.wireOp",EDGE,"E40.right"),sQuery(id+"F4.wireOp",EDGE,"E45.MirrorCS"),sQuery(id+"F4.wireOp",EDGE,"E46.MirrorCS"),sQuery(id+"F4.wireOp",EDGE,"E47.MirrorCS"),sQuery(id+"F4.wireOp",EDGE,"E48.MirrorCS"),sQuery(id+"F4.wireOp",EDGE,"E49.MirrorCS"),sQuery(id+"F4.wireOp",EDGE,"E50.bottom"),sQuery(id+"F4.wireOp",EDGE,"E51.top"),sQuery(id+"F4.wireOp",EDGE,"E51.right"),sQuery(id+"F4.wireOp",EDGE,"E52.MirrorCS"),sQuery(id+"F4.wireOp",EDGE,"E53.MirrorCS"),sQuery(id+"F4.wireOp",EDGE,"E54.top"),sQuery(id+"F4.wireOp",EDGE,"E54.left"),sQuery(id+"F4.wireOp",EDGE,"E55.MirrorCS"),sQuery(id+"F4.wireOp",EDGE,"E56.MirrorCS"),sQuery(id+"F4.wireOp",EDGE,"E57.top"),sQuery(id+"F4.wireOp",EDGE,"E57.right"),sQuery(id+"F4.wireOp",EDGE,"E58.MirrorCS"),sQuery(id+"F4.wireOp",EDGE,"E59.MirrorCS")])]}),"instanceName":"1"});
            deleteBodies(context, id + "F33", {"entities" : qUnion([Q0])});
        }
        {
            var Q0;
            Q0=qCreatedBy(makeId("Right.planeOp"),FACE);
            var sketch = newSketch(context, id + "F34", { "sketchPlane" : qUnion([Q0])});
            skLineSegment(sketch, "E142.bottom", {"start": v(-244.06, 237.28) * mm, "end": v(-129.76, 237.28) * mm});
            skLineSegment(sketch, "E142.top", {"start": v(-244.06, 291.25) * mm, "end": v(-129.76, 291.25) * mm});
            skLineSegment(sketch, "E142.left", {"start": v(-244.06, 237.28) * mm, "end": v(-244.06, 291.25) * mm});
            skLineSegment(sketch, "E142.right", {"start": v(-129.76, 237.28) * mm, "end": v(-129.76, 291.25) * mm});
            skLineSegment(sketch, "E143.bottom", {"start": v(-244.06, 237.28) * mm, "end": v(-237.71, 237.28) * mm});
            skLineSegment(sketch, "E143.top", {"start": v(-244.06, 249.98) * mm, "end": v(-237.71, 249.98) * mm});
            skLineSegment(sketch, "E143.left", {"start": v(-244.06, 237.28) * mm, "end": v(-244.06, 249.98) * mm});
            skLineSegment(sketch, "E143.right", {"start": v(-237.71, 237.28) * mm, "end": v(-237.71, 249.98) * mm});
            skLineSegment(sketch, "E144.bottom", {"start": v(-244.06, 275.38) * mm, "end": v(-237.71, 275.38) * mm});
            skLineSegment(sketch, "E144.top", {"start": v(-244.06, 262.68) * mm, "end": v(-237.71, 262.68) * mm});
            skLineSegment(sketch, "E144.left", {"start": v(-244.06, 275.38) * mm, "end": v(-244.06, 262.68) * mm});
            skLineSegment(sketch, "E144.right", {"start": v(-237.71, 275.38) * mm, "end": v(-237.71, 262.68) * mm});
            skLineSegment(sketch, "E145.bottom", {"start": v(-231.36, 291.25) * mm, "end": v(-218.66, 291.25) * mm});
            skLineSegment(sketch, "E145.top", {"start": v(-231.36, 284.9) * mm, "end": v(-218.66, 284.9) * mm});
            skLineSegment(sketch, "E145.left", {"start": v(-231.36, 291.25) * mm, "end": v(-231.36, 284.9) * mm});
            skLineSegment(sketch, "E145.right", {"start": v(-218.66, 291.25) * mm, "end": v(-218.66, 284.9) * mm});
            skLineSegment(sketch, "E146.1.0.0", {"start": v(-205.96, 291.25) * mm, "end": v(-205.96, 284.9) * mm});
            skLineSegment(sketch, "E146.1.0.1", {"start": v(-193.26, 291.25) * mm, "end": v(-193.26, 284.9) * mm});
            skLineSegment(sketch, "E146.1.0.2", {"start": v(-205.96, 291.25) * mm, "end": v(-193.26, 291.25) * mm});
            skLineSegment(sketch, "E146.1.0.3", {"start": v(-205.96, 284.9) * mm, "end": v(-193.26, 284.9) * mm});
            skLineSegment(sketch, "E146.2.0.0", {"start": v(-180.56, 291.25) * mm, "end": v(-180.56, 284.9) * mm});
            skLineSegment(sketch, "E146.2.0.1", {"start": v(-167.86, 291.25) * mm, "end": v(-167.86, 284.9) * mm});
            skLineSegment(sketch, "E146.2.0.2", {"start": v(-180.56, 291.25) * mm, "end": v(-167.86, 291.25) * mm});
            skLineSegment(sketch, "E146.2.0.3", {"start": v(-180.56, 284.9) * mm, "end": v(-167.86, 284.9) * mm});
            skLineSegment(sketch, "E146.3.0.0", {"start": v(-155.16, 291.25) * mm, "end": v(-155.16, 284.9) * mm});
            skLineSegment(sketch, "E146.3.0.1", {"start": v(-142.46, 291.25) * mm, "end": v(-142.46, 284.9) * mm});
            skLineSegment(sketch, "E146.3.0.2", {"start": v(-155.16, 291.25) * mm, "end": v(-142.46, 291.25) * mm});
            skLineSegment(sketch, "E146.3.0.3", {"start": v(-155.16, 284.9) * mm, "end": v(-142.46, 284.9) * mm});
            skLineSegment(sketch, "E146.direction1", {"start": v(-244.06, 291.25) * mm, "end": v(-218.66, 291.25) * mm, "construction": true});
            skLineSegment(sketch, "E147", {"start": v(-186.91, 291.25) * mm, "end": v(-186.91, 237.28) * mm, "construction": true});
            skLineSegment(sketch, "E148.MirrorCS", {"start": v(-129.76, 262.68) * mm, "end": v(-136.11, 262.68) * mm});
            skLineSegment(sketch, "E149.MirrorCS", {"start": v(-129.76, 275.38) * mm, "end": v(-136.11, 275.38) * mm});
            skLineSegment(sketch, "E150.MirrorCS", {"start": v(-136.11, 275.38) * mm, "end": v(-136.11, 262.68) * mm});
            skLineSegment(sketch, "E151.MirrorCS", {"start": v(-129.76, 249.98) * mm, "end": v(-136.11, 249.98) * mm});
            skLineSegment(sketch, "E152.MirrorCS", {"start": v(-136.11, 237.28) * mm, "end": v(-136.11, 249.98) * mm});
            skSolve(sketch);
        }
        {
            var Q0;
            {var subQ6=sQuery(id+"F34.wireOp",EDGE,"E143.top");Q0=makeQuery(id+"F34.imprint","IMPRINT",FACE,{"disambiguationData":[TD([[makeQuery(id+"F34.imprint","IMPRINT",EDGE,{"derivedFrom":subQ6}),1.0]])]});}
            extrude(context, id + "F35", {"entities" : qUnion([Q0]), "depth" : 6.35 * mm});
        }
        {
            var Q0;
            Q0=qCreatedBy(makeId("Right.planeOp"),FACE);
            var sketch = newSketch(context, id + "F36", { "sketchPlane" : qUnion([Q0])});
            skLineSegment(sketch, "E153.bottom", {"start": v(-83.94, 241.82) * mm, "end": v(-7.74, 241.82) * mm});
            skLineSegment(sketch, "E153.top", {"start": v(-83.94, 295.8) * mm, "end": v(-7.74, 295.8) * mm});
            skLineSegment(sketch, "E153.left", {"start": v(-83.94, 241.82) * mm, "end": v(-83.94, 295.8) * mm});
            skLineSegment(sketch, "E153.right", {"start": v(-7.74, 241.82) * mm, "end": v(-7.74, 295.8) * mm});
            skLineSegment(sketch, "E154.bottom", {"start": v(-83.94, 295.8) * mm, "end": v(-77.59, 295.8) * mm});
            skLineSegment(sketch, "E154.top", {"start": v(-83.94, 279.92) * mm, "end": v(-77.59, 279.92) * mm});
            skLineSegment(sketch, "E154.left", {"start": v(-83.94, 295.8) * mm, "end": v(-83.94, 279.92) * mm});
            skLineSegment(sketch, "E154.right", {"start": v(-77.59, 295.8) * mm, "end": v(-77.59, 279.92) * mm});
            skLineSegment(sketch, "E155.bottom", {"start": v(-83.94, 254.52) * mm, "end": v(-77.59, 254.52) * mm});
            skLineSegment(sketch, "E155.top", {"start": v(-83.94, 267.22) * mm, "end": v(-77.59, 267.22) * mm});
            skLineSegment(sketch, "E155.left", {"start": v(-83.94, 254.52) * mm, "end": v(-83.94, 267.22) * mm});
            skLineSegment(sketch, "E155.right", {"start": v(-77.59, 254.52) * mm, "end": v(-77.59, 267.22) * mm});
            skLineSegment(sketch, "E156.bottom", {"start": v(-64.89, 295.8) * mm, "end": v(-52.19, 295.8) * mm});
            skLineSegment(sketch, "E156.top", {"start": v(-64.89, 289.44) * mm, "end": v(-52.19, 289.44) * mm});
            skLineSegment(sketch, "E156.left", {"start": v(-64.89, 295.8) * mm, "end": v(-64.89, 289.44) * mm});
            skLineSegment(sketch, "E156.right", {"start": v(-52.19, 295.8) * mm, "end": v(-52.19, 289.44) * mm});
            skLineSegment(sketch, "E157.1.0.0", {"start": v(-26.79, 295.8) * mm, "end": v(-26.79, 289.44) * mm});
            skLineSegment(sketch, "E157.1.0.1", {"start": v(-39.49, 289.44) * mm, "end": v(-26.79, 289.44) * mm});
            skLineSegment(sketch, "E157.1.0.2", {"start": v(-39.49, 295.8) * mm, "end": v(-39.49, 289.44) * mm});
            skLineSegment(sketch, "E157.direction1", {"start": v(-64.89, 289.44) * mm, "end": v(-39.49, 289.44) * mm, "construction": true});
            skLineSegment(sketch, "E158", {"start": v(-45.84, 241.82) * mm, "end": v(-45.84, 295.8) * mm, "construction": true});
            skLineSegment(sketch, "E159.MirrorCS", {"start": v(-7.74, 254.52) * mm, "end": v(-14.09, 254.52) * mm});
            skLineSegment(sketch, "E160.MirrorCS", {"start": v(-7.74, 267.22) * mm, "end": v(-14.09, 267.22) * mm});
            skLineSegment(sketch, "E161.MirrorCS", {"start": v(-7.74, 279.92) * mm, "end": v(-14.09, 279.92) * mm});
            skLineSegment(sketch, "E162.MirrorCS", {"start": v(-14.09, 295.8) * mm, "end": v(-14.09, 279.92) * mm});
            skLineSegment(sketch, "E163.MirrorCS", {"start": v(-14.09, 254.52) * mm, "end": v(-14.09, 267.22) * mm});
            skSolve(sketch);
        }
        {
            var Q0;
            {var subQ13=sQuery(id+"F36.wireOp",EDGE,"E153.bottom");Q0=makeQuery(id+"F36.imprint","IMPRINT",FACE,{"disambiguationData":[TD([[makeQuery(id+"F36.imprint","IMPRINT",EDGE,{"derivedFrom":subQ13}),1.0]])]});}
            extrude(context, id + "F37", {"entities" : qUnion([Q0]), "depth" : 6.35 * mm});
        }
        {
            var Q0;
            Q0=qCreatedBy(makeId("Right.planeOp"),FACE);
            var sketch = newSketch(context, id + "F38", { "sketchPlane" : qUnion([Q0])});
            skLineSegment(sketch, "E164.bottom", {"start": v(-505.29, 353.03) * mm, "end": v(-390.99, 353.03) * mm});
            skLineSegment(sketch, "E164.top", {"start": v(-505.29, 429.23) * mm, "end": v(-390.99, 429.23) * mm});
            skLineSegment(sketch, "E164.left", {"start": v(-505.29, 353.03) * mm, "end": v(-505.29, 429.23) * mm});
            skLineSegment(sketch, "E164.right", {"start": v(-390.99, 353.03) * mm, "end": v(-390.99, 429.23) * mm});
            skLineSegment(sketch, "E165.bottom", {"start": v(-505.29, 429.23) * mm, "end": v(-492.59, 429.23) * mm});
            skLineSegment(sketch, "E165.top", {"start": v(-505.29, 422.88) * mm, "end": v(-492.59, 422.88) * mm});
            skLineSegment(sketch, "E165.left", {"start": v(-505.29, 429.23) * mm, "end": v(-505.29, 422.88) * mm});
            skLineSegment(sketch, "E165.right", {"start": v(-492.59, 429.23) * mm, "end": v(-492.59, 422.88) * mm});
            skLineSegment(sketch, "E166", {"start": v(-448.14, 429.23) * mm, "end": v(-448.14, 353.03) * mm, "construction": true});
            skLineSegment(sketch, "E167.1.0.0", {"start": v(-467.19, 429.23) * mm, "end": v(-467.19, 422.88) * mm});
            skLineSegment(sketch, "E167.1.0.1", {"start": v(-479.89, 422.88) * mm, "end": v(-467.19, 422.88) * mm});
            skLineSegment(sketch, "E167.1.0.2", {"start": v(-479.89, 429.23) * mm, "end": v(-467.19, 429.23) * mm});
            skLineSegment(sketch, "E167.1.0.3", {"start": v(-479.89, 429.23) * mm, "end": v(-479.89, 422.88) * mm});
            skLineSegment(sketch, "E167.2.0.0", {"start": v(-441.79, 429.23) * mm, "end": v(-441.79, 422.88) * mm});
            skLineSegment(sketch, "E167.2.0.1", {"start": v(-454.49, 422.88) * mm, "end": v(-441.79, 422.88) * mm});
            skLineSegment(sketch, "E167.2.0.2", {"start": v(-454.49, 429.23) * mm, "end": v(-441.79, 429.23) * mm});
            skLineSegment(sketch, "E167.2.0.3", {"start": v(-454.49, 429.23) * mm, "end": v(-454.49, 422.88) * mm});
            skLineSegment(sketch, "E167.3.0.0", {"start": v(-416.39, 429.23) * mm, "end": v(-416.39, 422.88) * mm});
            skLineSegment(sketch, "E167.3.0.1", {"start": v(-429.09, 422.88) * mm, "end": v(-416.39, 422.88) * mm});
            skLineSegment(sketch, "E167.3.0.2", {"start": v(-429.09, 429.23) * mm, "end": v(-416.39, 429.23) * mm});
            skLineSegment(sketch, "E167.3.0.3", {"start": v(-429.09, 429.23) * mm, "end": v(-429.09, 422.88) * mm});
            skLineSegment(sketch, "E167.4.0.0", {"start": v(-390.99, 429.23) * mm, "end": v(-390.99, 422.88) * mm});
            skLineSegment(sketch, "E167.4.0.1", {"start": v(-403.69, 422.88) * mm, "end": v(-390.99, 422.88) * mm});
            skLineSegment(sketch, "E167.4.0.2", {"start": v(-403.69, 429.23) * mm, "end": v(-390.99, 429.23) * mm});
            skLineSegment(sketch, "E167.4.0.3", {"start": v(-403.69, 429.23) * mm, "end": v(-403.69, 422.88) * mm});
            skLineSegment(sketch, "E167.direction1", {"start": v(-505.29, 422.88) * mm, "end": v(-479.89, 422.88) * mm, "construction": true});
            skPoint(sketch, "E168.oppositeSnap0", {"position": v(-498.94, 422.88) * mm});
            skLineSegment(sketch, "E168.bottom", {"start": v(-505.29, 359.38) * mm, "end": v(-498.94, 359.38) * mm});
            skLineSegment(sketch, "E168.top", {"start": v(-505.29, 372.08) * mm, "end": v(-498.94, 372.08) * mm});
            skLineSegment(sketch, "E168.left", {"start": v(-505.29, 359.38) * mm, "end": v(-505.29, 372.08) * mm});
            skLineSegment(sketch, "E168.right", {"start": v(-498.94, 359.38) * mm, "end": v(-498.94, 372.08) * mm});
            skLineSegment(sketch, "E169.0.1.0", {"start": v(-498.94, 384.78) * mm, "end": v(-498.94, 397.48) * mm});
            skLineSegment(sketch, "E169.0.1.1", {"start": v(-505.29, 384.78) * mm, "end": v(-498.94, 384.78) * mm});
            skLineSegment(sketch, "E169.0.1.2", {"start": v(-505.29, 397.48) * mm, "end": v(-498.94, 397.48) * mm});
            skLineSegment(sketch, "E169.0.1.3", {"start": v(-505.29, 384.78) * mm, "end": v(-505.29, 397.48) * mm});
            skLineSegment(sketch, "E169.0.2.0", {"start": v(-498.94, 410.18) * mm, "end": v(-498.94, 422.88) * mm});
            skLineSegment(sketch, "E169.0.2.1", {"start": v(-505.29, 410.18) * mm, "end": v(-498.94, 410.18) * mm});
            skLineSegment(sketch, "E169.0.2.2", {"start": v(-505.29, 422.88) * mm, "end": v(-498.94, 422.88) * mm});
            skLineSegment(sketch, "E169.0.2.3", {"start": v(-505.29, 410.18) * mm, "end": v(-505.29, 422.88) * mm});
            skLineSegment(sketch, "E169.direction1", {"start": v(-505.29, 359.38) * mm, "end": v(-479.89, 359.38) * mm, "construction": true});
            skLineSegment(sketch, "E169.direction2", {"start": v(-505.29, 359.38) * mm, "end": v(-505.29, 384.78) * mm, "construction": true});
            skLineSegment(sketch, "E170", {"start": v(-505.29, 391.13) * mm, "end": v(-390.99, 391.13) * mm, "construction": true});
            skLineSegment(sketch, "E171.MirrorCS", {"start": v(-505.29, 359.38) * mm, "end": v(-492.59, 359.38) * mm});
            skLineSegment(sketch, "E172.MirrorCS", {"start": v(-479.89, 359.38) * mm, "end": v(-467.19, 359.38) * mm});
            skLineSegment(sketch, "E173.MirrorCS", {"start": v(-467.19, 353.03) * mm, "end": v(-467.19, 359.38) * mm});
            skLineSegment(sketch, "E174.MirrorCS", {"start": v(-479.89, 353.03) * mm, "end": v(-479.89, 359.38) * mm});
            skLineSegment(sketch, "E175.MirrorCS", {"start": v(-429.09, 359.38) * mm, "end": v(-416.39, 359.38) * mm});
            skLineSegment(sketch, "E176.MirrorCS", {"start": v(-492.59, 353.03) * mm, "end": v(-492.59, 359.38) * mm});
            skLineSegment(sketch, "E177.MirrorCS", {"start": v(-403.69, 359.38) * mm, "end": v(-390.99, 359.38) * mm});
            skLineSegment(sketch, "E178.MirrorCS", {"start": v(-416.39, 353.03) * mm, "end": v(-416.39, 359.38) * mm});
            skLineSegment(sketch, "E179.MirrorCS", {"start": v(-441.79, 353.03) * mm, "end": v(-441.79, 359.38) * mm});
            skLineSegment(sketch, "E180.MirrorCS", {"start": v(-429.09, 353.03) * mm, "end": v(-429.09, 359.38) * mm});
            skLineSegment(sketch, "E181.MirrorCS", {"start": v(-454.49, 359.38) * mm, "end": v(-441.79, 359.38) * mm});
            skLineSegment(sketch, "E182.MirrorCS", {"start": v(-448.14, 353.03) * mm, "end": v(-448.14, 429.23) * mm, "construction": true});
            skLineSegment(sketch, "E183.MirrorCS", {"start": v(-403.69, 353.03) * mm, "end": v(-403.69, 359.38) * mm});
            skLineSegment(sketch, "E184.MirrorCS", {"start": v(-454.49, 353.03) * mm, "end": v(-454.49, 359.38) * mm});
            skLineSegment(sketch, "E185.MirrorCS", {"start": v(-390.99, 384.78) * mm, "end": v(-397.34, 384.78) * mm});
            skLineSegment(sketch, "E186.MirrorCS", {"start": v(-397.34, 359.38) * mm, "end": v(-397.34, 372.08) * mm});
            skLineSegment(sketch, "E187.MirrorCS", {"start": v(-390.99, 397.48) * mm, "end": v(-397.34, 397.48) * mm});
            skLineSegment(sketch, "E188.MirrorCS", {"start": v(-390.99, 391.13) * mm, "end": v(-505.29, 391.13) * mm, "construction": true});
            skLineSegment(sketch, "E189.MirrorCS", {"start": v(-397.34, 384.78) * mm, "end": v(-397.34, 397.48) * mm});
            skLineSegment(sketch, "E190.MirrorCS", {"start": v(-390.99, 410.18) * mm, "end": v(-397.34, 410.18) * mm});
            skLineSegment(sketch, "E191.MirrorCS", {"start": v(-397.34, 410.18) * mm, "end": v(-397.34, 422.88) * mm});
            skLineSegment(sketch, "E192.MirrorCS", {"start": v(-390.99, 372.08) * mm, "end": v(-397.34, 372.08) * mm});
            skPoint(sketch, "E193.firstSnap0", {"position": v(-448.14, 359.38) * mm});
            skLineSegment(sketch, "E193.bottom", {"start": v(-448.14, 327.63) * mm, "end": v(-143.34, 327.63) * mm});
            skLineSegment(sketch, "E193.top", {"start": v(-448.14, 454.63) * mm, "end": v(-143.34, 454.63) * mm});
            skLineSegment(sketch, "E193.left", {"start": v(-448.14, 327.63) * mm, "end": v(-448.14, 454.63) * mm});
            skLineSegment(sketch, "E193.right", {"start": v(-143.34, 327.63) * mm, "end": v(-143.34, 454.63) * mm});
            skLineSegment(sketch, "E194", {"start": v(-295.74, 454.63) * mm, "end": v(-295.74, 327.63) * mm, "construction": true});
            skLineSegment(sketch, "E195.MirrorCS", {"start": v(-149.69, 429.23) * mm, "end": v(-149.69, 422.88) * mm});
            skLineSegment(sketch, "E196.MirrorCS", {"start": v(-187.79, 429.23) * mm, "end": v(-187.79, 422.88) * mm});
            skLineSegment(sketch, "E197.MirrorCS", {"start": v(-175.09, 429.23) * mm, "end": v(-175.09, 422.88) * mm});
            skLineSegment(sketch, "E198.MirrorCS", {"start": v(-162.39, 429.23) * mm, "end": v(-162.39, 422.88) * mm});
            skLineSegment(sketch, "E199.MirrorCS", {"start": v(-200.49, 429.23) * mm, "end": v(-200.49, 422.88) * mm});
            skLineSegment(sketch, "E200.MirrorCS", {"start": v(-187.79, 422.88) * mm, "end": v(-200.49, 422.88) * mm});
            skLineSegment(sketch, "E201.MirrorCS", {"start": v(-187.79, 353.03) * mm, "end": v(-187.79, 359.38) * mm});
            skLineSegment(sketch, "E202.MirrorCS", {"start": v(-187.79, 359.38) * mm, "end": v(-200.49, 359.38) * mm});
            skLineSegment(sketch, "E203.MirrorCS", {"start": v(-200.49, 410.18) * mm, "end": v(-194.14, 410.18) * mm});
            skLineSegment(sketch, "E204.MirrorCS", {"start": v(-200.49, 397.48) * mm, "end": v(-194.14, 397.48) * mm});
            skLineSegment(sketch, "E205.MirrorCS", {"start": v(-200.49, 384.78) * mm, "end": v(-194.14, 384.78) * mm});
            skLineSegment(sketch, "E206.MirrorCS", {"start": v(-175.09, 353.03) * mm, "end": v(-175.09, 359.38) * mm});
            skLineSegment(sketch, "E207.MirrorCS", {"start": v(-162.39, 353.03) * mm, "end": v(-162.39, 359.38) * mm});
            skLineSegment(sketch, "E208.MirrorCS", {"start": v(-149.69, 353.03) * mm, "end": v(-149.69, 359.38) * mm});
            skLineSegment(sketch, "E209.MirrorCS", {"start": v(-200.49, 372.08) * mm, "end": v(-194.14, 372.08) * mm});
            skLineSegment(sketch, "E210.MirrorCS", {"start": v(-194.14, 384.78) * mm, "end": v(-194.14, 397.48) * mm});
            skLineSegment(sketch, "E211.MirrorCS", {"start": v(-187.79, 429.23) * mm, "end": v(-200.49, 429.23) * mm});
            skLineSegment(sketch, "E212.MirrorCS", {"start": v(-162.39, 359.38) * mm, "end": v(-175.09, 359.38) * mm});
            skLineSegment(sketch, "E213.MirrorCS", {"start": v(-194.14, 359.38) * mm, "end": v(-194.14, 372.08) * mm});
            skLineSegment(sketch, "E214.MirrorCS", {"start": v(-194.14, 410.18) * mm, "end": v(-194.14, 422.88) * mm});
            skLineSegment(sketch, "E215.MirrorCS", {"start": v(-200.49, 353.03) * mm, "end": v(-200.49, 429.23) * mm});
            skLineSegment(sketch, "E216.MirrorCS", {"start": v(-162.39, 429.23) * mm, "end": v(-175.09, 429.23) * mm});
            skLineSegment(sketch, "E217.MirrorCS", {"start": v(-162.39, 422.88) * mm, "end": v(-175.09, 422.88) * mm});
            skLineSegment(sketch, "E218.MirrorCS", {"start": v(-136.99, 359.38) * mm, "end": v(-149.69, 359.38) * mm});
            skLineSegment(sketch, "E219.MirrorCS", {"start": v(-143.34, 422.88) * mm, "end": v(-149.69, 422.88) * mm});
            skLineSegment(sketch, "E220.MirrorCS", {"start": v(-86.19, 353.03) * mm, "end": v(-200.49, 353.03) * mm});
            skLineSegment(sketch, "E221", {"start": v(-149.69, 429.23) * mm, "end": v(-143.34, 429.23) * mm});
            skLineSegment(sketch, "E222", {"start": v(-143.34, 429.23) * mm, "end": v(-143.34, 422.88) * mm});
            skPoint(sketch, "E223.orphan", {"position": v(-136.99, 422.88) * mm});
            skSolve(sketch);
        }
        {
            var Q0;
            {var subQ16=sQuery(id+"F38.wireOp",EDGE,"E167.3.0.2");Q0=makeQuery(id+"F38.imprint","IMPRINT",FACE,{"disambiguationData":[TD([[makeQuery(id+"F38.imprint","IMPRINT",EDGE,{"derivedFrom":subQ16}),1.0]])]});}
            var Q1;
            {var subQ7=sQuery(id+"F38.wireOp",EDGE,"E167.2.0.0");Q1=makeQuery(id+"F38.imprint","IMPRINT",FACE,{"disambiguationData":[TD([[makeQuery(id+"F38.imprint","IMPRINT",EDGE,{"derivedFrom":subQ7}),1.0]])]});}
            extrude(context, id + "F39", {"entities" : qUnion([Q0, Q1]), "depth" : 6.35 * mm});
        }
        {
            var Q0;
            Q0=qCreatedBy(makeId("Right.planeOp"),FACE);
            var sketch = newSketch(context, id + "F40", { "sketchPlane" : qUnion([Q0])});
            skLineSegment(sketch, "E224.left", {"start": v(-684.86, 283.5) * mm, "end": v(-684.86, 410.5) * mm});
            skLineSegment(sketch, "E225.bottom", {"start": v(-684.86, 410.5) * mm, "end": v(-691.2, 410.5) * mm});
            skLineSegment(sketch, "E225.left", {"start": v(-684.86, 410.5) * mm, "end": v(-684.86, 404.14) * mm});
            skLineSegment(sketch, "E226.left", {"start": v(-684.86, 391.44) * mm, "end": v(-684.86, 378.74) * mm});
            skLineSegment(sketch, "E227.bottom", {"start": v(-684.86, 410.5) * mm, "end": v(-1065.86, 410.5) * mm});
            skLineSegment(sketch, "E227.top", {"start": v(-684.86, 283.5) * mm, "end": v(-1065.86, 283.5) * mm});
            skLineSegment(sketch, "E227.left", {"start": v(-684.86, 410.5) * mm, "end": v(-684.86, 283.5) * mm});
            skLineSegment(sketch, "E227.right", {"start": v(-1065.86, 410.5) * mm, "end": v(-1065.86, 283.5) * mm});
            skLineSegment(sketch, "E228.bottom", {"start": v(-1065.86, 385.1) * mm, "end": v(-1008.7, 385.1) * mm});
            skLineSegment(sketch, "E228.top", {"start": v(-1065.86, 308.9) * mm, "end": v(-1008.7, 308.9) * mm});
            skLineSegment(sketch, "E228.left", {"start": v(-1065.86, 385.1) * mm, "end": v(-1065.86, 308.9) * mm});
            skLineSegment(sketch, "E228.right", {"start": v(-1008.7, 385.1) * mm, "end": v(-1008.7, 308.9) * mm});
            skLineSegment(sketch, "E229.bottom", {"start": v(-1008.7, 385.1) * mm, "end": v(-1015.06, 385.1) * mm});
            skLineSegment(sketch, "E229.top", {"start": v(-1008.7, 366.04) * mm, "end": v(-1015.06, 366.04) * mm});
            skLineSegment(sketch, "E229.left", {"start": v(-1008.7, 385.1) * mm, "end": v(-1008.7, 366.04) * mm});
            skLineSegment(sketch, "E229.right", {"start": v(-1015.06, 385.1) * mm, "end": v(-1015.06, 366.04) * mm});
            skLineSegment(sketch, "E230.bottom", {"start": v(-1008.7, 353.34) * mm, "end": v(-1015.06, 353.34) * mm});
            skLineSegment(sketch, "E230.top", {"start": v(-1008.7, 340.64) * mm, "end": v(-1015.06, 340.64) * mm});
            skLineSegment(sketch, "E230.left", {"start": v(-1008.7, 353.34) * mm, "end": v(-1008.7, 340.64) * mm});
            skLineSegment(sketch, "E230.right", {"start": v(-1015.06, 353.34) * mm, "end": v(-1015.06, 340.64) * mm});
            skLineSegment(sketch, "E231.bottom", {"start": v(-1008.7, 385.1) * mm, "end": v(-1021.4, 385.1) * mm});
            skLineSegment(sketch, "E231.top", {"start": v(-1008.7, 378.74) * mm, "end": v(-1021.4, 378.74) * mm});
            skLineSegment(sketch, "E231.left", {"start": v(-1008.7, 385.1) * mm, "end": v(-1008.7, 378.74) * mm});
            skLineSegment(sketch, "E231.right", {"start": v(-1021.4, 385.1) * mm, "end": v(-1021.4, 378.74) * mm});
            skLineSegment(sketch, "E232.bottom", {"start": v(-1034.1, 385.1) * mm, "end": v(-1046.8, 385.1) * mm});
            skLineSegment(sketch, "E232.top", {"start": v(-1034.1, 378.74) * mm, "end": v(-1046.8, 378.74) * mm});
            skLineSegment(sketch, "E232.left", {"start": v(-1034.1, 385.1) * mm, "end": v(-1034.1, 378.74) * mm});
            skLineSegment(sketch, "E232.right", {"start": v(-1046.8, 385.1) * mm, "end": v(-1046.8, 378.74) * mm});
            skLineSegment(sketch, "E233.bottom", {"start": v(-1065.86, 385.1) * mm, "end": v(-1059.5, 385.1) * mm});
            skLineSegment(sketch, "E233.top", {"start": v(-1065.86, 378.74) * mm, "end": v(-1059.5, 378.74) * mm});
            skLineSegment(sketch, "E233.left", {"start": v(-1065.86, 385.1) * mm, "end": v(-1065.86, 378.74) * mm});
            skLineSegment(sketch, "E233.right", {"start": v(-1059.5, 385.1) * mm, "end": v(-1059.5, 378.74) * mm});
            skLineSegment(sketch, "E234", {"start": v(-1008.7, 347) * mm, "end": v(-1065.86, 347) * mm, "construction": true});
            skLineSegment(sketch, "E235.MirrorCS", {"start": v(-1034.1, 308.9) * mm, "end": v(-1034.1, 315.24) * mm});
            skLineSegment(sketch, "E236.MirrorCS", {"start": v(-1015.06, 308.9) * mm, "end": v(-1015.06, 327.94) * mm});
            skLineSegment(sketch, "E237.MirrorCS", {"start": v(-1046.8, 308.9) * mm, "end": v(-1046.8, 315.24) * mm});
            skLineSegment(sketch, "E238.MirrorCS", {"start": v(-1021.4, 308.9) * mm, "end": v(-1021.4, 315.24) * mm});
            skLineSegment(sketch, "E239.MirrorCS", {"start": v(-1034.1, 315.24) * mm, "end": v(-1046.8, 315.24) * mm});
            skLineSegment(sketch, "E240.MirrorCS", {"start": v(-1008.7, 315.24) * mm, "end": v(-1021.4, 315.24) * mm});
            skLineSegment(sketch, "E241.MirrorCS", {"start": v(-1065.86, 315.24) * mm, "end": v(-1059.5, 315.24) * mm});
            skLineSegment(sketch, "E242.MirrorCS", {"start": v(-1059.5, 308.9) * mm, "end": v(-1059.5, 315.24) * mm});
            skLineSegment(sketch, "E243.MirrorCS", {"start": v(-1008.7, 327.94) * mm, "end": v(-1015.06, 327.94) * mm});
            skLineSegment(sketch, "E244.bottom", {"start": v(-1062.68, 347) * mm, "end": v(-1069.03, 347) * mm});
            skLineSegment(sketch, "E244.top", {"start": v(-1062.68, 359.7) * mm, "end": v(-1069.03, 359.7) * mm});
            skLineSegment(sketch, "E244.left", {"start": v(-1062.68, 347) * mm, "end": v(-1062.68, 359.7) * mm});
            skLineSegment(sketch, "E244.right", {"start": v(-1069.03, 347) * mm, "end": v(-1069.03, 359.7) * mm});
            skLineSegment(sketch, "E245.MirrorCS", {"start": v(-1062.68, 334.3) * mm, "end": v(-1069.03, 334.3) * mm});
            skLineSegment(sketch, "E246.MirrorCS", {"start": v(-1062.68, 347) * mm, "end": v(-1062.68, 334.3) * mm});
            skLineSegment(sketch, "E247", {"start": v(-1065.86, 359.7) * mm, "end": v(-1008.7, 359.7) * mm, "construction": true});
            skLineSegment(sketch, "E248", {"start": v(-1065.86, 334.3) * mm, "end": v(-1008.7, 334.3) * mm, "construction": true});
            skLineSegment(sketch, "E249", {"start": v(-1069.03, 347) * mm, "end": v(-1069.03, 334.3) * mm});
            skLineSegment(sketch, "E250.MirrorCS", {"start": v(-1065.86, 258.1) * mm, "end": v(-1065.86, 385.1) * mm});
            skLineSegment(sketch, "E251.MirrorCS", {"start": v(-1069.03, 321.6) * mm, "end": v(-1069.03, 334.3) * mm});
            skLineSegment(sketch, "E252.MirrorCS", {"start": v(-1069.03, 321.6) * mm, "end": v(-1069.03, 308.9) * mm});
            skLineSegment(sketch, "E253.MirrorCS", {"start": v(-1062.68, 308.9) * mm, "end": v(-1069.03, 308.9) * mm});
            skLineSegment(sketch, "E254.MirrorCS", {"start": v(-1065.86, 308.9) * mm, "end": v(-1008.7, 308.9) * mm, "construction": true});
            skLineSegment(sketch, "E255.MirrorCS", {"start": v(-1008.7, 321.6) * mm, "end": v(-1065.86, 321.6) * mm, "construction": true});
            skLineSegment(sketch, "E256.MirrorCS", {"start": v(-1062.68, 321.6) * mm, "end": v(-1062.68, 334.3) * mm});
            skLineSegment(sketch, "E257.MirrorCS", {"start": v(-1062.68, 321.6) * mm, "end": v(-1069.03, 321.6) * mm});
            skLineSegment(sketch, "E258.MirrorCS", {"start": v(-1065.86, 283.5) * mm, "end": v(-1065.86, 359.7) * mm});
            skLineSegment(sketch, "E259.MirrorCS", {"start": v(-1062.68, 321.6) * mm, "end": v(-1062.68, 308.9) * mm});
            skLineSegment(sketch, "E260.MirrorCS", {"start": v(-1065.86, 308.9) * mm, "end": v(-1065.86, 435.9) * mm});
            skLineSegment(sketch, "E261.MirrorCS", {"start": v(-1065.86, 435.9) * mm, "end": v(-1065.86, 359.7) * mm});
            skLineSegment(sketch, "E262.MirrorCS", {"start": v(-1065.86, 461.3) * mm, "end": v(-1065.86, 334.3) * mm});
            skLineSegment(sketch, "E263.MirrorCS", {"start": v(-1062.68, 372.4) * mm, "end": v(-1069.03, 372.4) * mm});
            skLineSegment(sketch, "E264.MirrorCS", {"start": v(-1069.03, 372.4) * mm, "end": v(-1069.03, 359.7) * mm});
            skLineSegment(sketch, "E265.MirrorCS", {"start": v(-1065.86, 334.3) * mm, "end": v(-1065.86, 410.5) * mm});
            skLineSegment(sketch, "E266.MirrorCS", {"start": v(-1069.03, 372.4) * mm, "end": v(-1069.03, 385.1) * mm});
            skLineSegment(sketch, "E267.MirrorCS", {"start": v(-1008.7, 372.4) * mm, "end": v(-1065.86, 372.4) * mm, "construction": true});
            skLineSegment(sketch, "E268.MirrorCS", {"start": v(-1062.68, 372.4) * mm, "end": v(-1062.68, 359.7) * mm});
            skLineSegment(sketch, "E269.MirrorCS", {"start": v(-1062.68, 372.4) * mm, "end": v(-1062.68, 385.1) * mm});
            skLineSegment(sketch, "E270.MirrorCS", {"start": v(-1062.68, 385.1) * mm, "end": v(-1069.03, 385.1) * mm});
            skLineSegment(sketch, "E271", {"start": v(-875.36, 410.5) * mm, "end": v(-875.36, 283.5) * mm, "construction": true});
            skLineSegment(sketch, "E272.MirrorCS", {"start": v(-703.9, 385.1) * mm, "end": v(-703.9, 378.74) * mm});
            skLineSegment(sketch, "E273.MirrorCS", {"start": v(-742, 366.04) * mm, "end": v(-735.66, 366.04) * mm});
            skLineSegment(sketch, "E274.MirrorCS", {"start": v(-716.6, 385.1) * mm, "end": v(-716.6, 378.74) * mm});
            skLineSegment(sketch, "E275.MirrorCS", {"start": v(-742, 385.1) * mm, "end": v(-729.3, 385.1) * mm});
            skLineSegment(sketch, "E276.MirrorCS", {"start": v(-742, 340.64) * mm, "end": v(-735.66, 340.64) * mm});
            skLineSegment(sketch, "E277.MirrorCS", {"start": v(-729.3, 385.1) * mm, "end": v(-729.3, 378.74) * mm});
            skLineSegment(sketch, "E278.MirrorCS", {"start": v(-742, 353.34) * mm, "end": v(-735.66, 353.34) * mm});
            skLineSegment(sketch, "E279.MirrorCS", {"start": v(-742, 385.1) * mm, "end": v(-742, 366.04) * mm});
            skLineSegment(sketch, "E280.MirrorCS", {"start": v(-742, 385.1) * mm, "end": v(-742, 378.74) * mm});
            skLineSegment(sketch, "E281.MirrorCS", {"start": v(-742, 385.1) * mm, "end": v(-735.66, 385.1) * mm});
            skLineSegment(sketch, "E282.MirrorCS", {"start": v(-742, 353.34) * mm, "end": v(-742, 340.64) * mm});
            skLineSegment(sketch, "E283.MirrorCS", {"start": v(-684.86, 308.9) * mm, "end": v(-742, 308.9) * mm});
            skLineSegment(sketch, "E284.MirrorCS", {"start": v(-729.3, 308.9) * mm, "end": v(-729.3, 315.24) * mm});
            skLineSegment(sketch, "E285.MirrorCS", {"start": v(-716.6, 308.9) * mm, "end": v(-716.6, 315.24) * mm});
            skLineSegment(sketch, "E286.MirrorCS", {"start": v(-703.9, 308.9) * mm, "end": v(-703.9, 315.24) * mm});
            skLineSegment(sketch, "E287.MirrorCS", {"start": v(-742, 327.94) * mm, "end": v(-735.66, 327.94) * mm});
            skLineSegment(sketch, "E288.MirrorCS", {"start": v(-742, 385.1) * mm, "end": v(-742, 308.9) * mm});
            skLineSegment(sketch, "E289.MirrorCS", {"start": v(-735.66, 308.9) * mm, "end": v(-735.66, 327.94) * mm});
            skLineSegment(sketch, "E290.MirrorCS", {"start": v(-742, 347) * mm, "end": v(-684.86, 347) * mm, "construction": true});
            skLineSegment(sketch, "E291.MirrorCS", {"start": v(-716.6, 315.24) * mm, "end": v(-703.9, 315.24) * mm});
            skLineSegment(sketch, "E292.MirrorCS", {"start": v(-742, 372.4) * mm, "end": v(-684.86, 372.4) * mm, "construction": true});
            skLineSegment(sketch, "E293.MirrorCS", {"start": v(-735.66, 353.34) * mm, "end": v(-735.66, 340.64) * mm});
            skLineSegment(sketch, "E294.MirrorCS", {"start": v(-684.86, 385.1) * mm, "end": v(-742, 385.1) * mm});
            skLineSegment(sketch, "E295.MirrorCS", {"start": v(-735.66, 385.1) * mm, "end": v(-735.66, 366.04) * mm});
            skLineSegment(sketch, "E296.MirrorCS", {"start": v(-742, 321.6) * mm, "end": v(-684.86, 321.6) * mm, "construction": true});
            skLineSegment(sketch, "E297.MirrorCS", {"start": v(-684.86, 359.7) * mm, "end": v(-742, 359.7) * mm, "construction": true});
            skLineSegment(sketch, "E298.MirrorCS", {"start": v(-684.86, 308.9) * mm, "end": v(-742, 308.9) * mm, "construction": true});
            skLineSegment(sketch, "E299.MirrorCS", {"start": v(-742, 378.74) * mm, "end": v(-729.3, 378.74) * mm});
            skLineSegment(sketch, "E300.MirrorCS", {"start": v(-742, 315.24) * mm, "end": v(-729.3, 315.24) * mm});
            skLineSegment(sketch, "E301.MirrorCS", {"start": v(-716.6, 378.74) * mm, "end": v(-703.9, 378.74) * mm});
            skLineSegment(sketch, "E302.MirrorCS", {"start": v(-716.6, 385.1) * mm, "end": v(-703.9, 385.1) * mm});
            skLineSegment(sketch, "E303.MirrorCS", {"start": v(-684.86, 334.3) * mm, "end": v(-742, 334.3) * mm, "construction": true});
            skLineSegment(sketch, "E304.MirrorCS", {"start": v(-688.03, 334.3) * mm, "end": v(-681.68, 334.3) * mm});
            skLineSegment(sketch, "E305.MirrorCS", {"start": v(-688.03, 359.7) * mm, "end": v(-681.68, 359.7) * mm});
            skLineSegment(sketch, "E306.MirrorCS", {"start": v(-688.03, 385.1) * mm, "end": v(-681.68, 385.1) * mm});
            skLineSegment(sketch, "E307.MirrorCS", {"start": v(-688.03, 321.6) * mm, "end": v(-681.68, 321.6) * mm});
            skLineSegment(sketch, "E308.MirrorCS", {"start": v(-688.03, 308.9) * mm, "end": v(-681.68, 308.9) * mm});
            skLineSegment(sketch, "E309.MirrorCS", {"start": v(-688.03, 372.4) * mm, "end": v(-681.68, 372.4) * mm});
            skLineSegment(sketch, "E310.MirrorCS", {"start": v(-684.86, 385.1) * mm, "end": v(-691.2, 385.1) * mm});
            skLineSegment(sketch, "E311.MirrorCS", {"start": v(-688.03, 347) * mm, "end": v(-681.68, 347) * mm});
            skLineSegment(sketch, "E312.MirrorCS", {"start": v(-691.2, 385.1) * mm, "end": v(-691.2, 378.74) * mm});
            skLineSegment(sketch, "E313.MirrorCS", {"start": v(-688.03, 372.4) * mm, "end": v(-688.03, 385.1) * mm});
            skLineSegment(sketch, "E314.MirrorCS", {"start": v(-688.03, 321.6) * mm, "end": v(-688.03, 308.9) * mm});
            skLineSegment(sketch, "E315.MirrorCS", {"start": v(-684.86, 385.1) * mm, "end": v(-684.86, 378.74) * mm});
            skLineSegment(sketch, "E316.MirrorCS", {"start": v(-684.86, 378.74) * mm, "end": v(-691.2, 378.74) * mm});
            skLineSegment(sketch, "E317.MirrorCS", {"start": v(-691.2, 308.9) * mm, "end": v(-691.2, 315.24) * mm});
            skLineSegment(sketch, "E318.MirrorCS", {"start": v(-684.86, 315.24) * mm, "end": v(-691.2, 315.24) * mm});
            skLineSegment(sketch, "E319.MirrorCS", {"start": v(-688.03, 372.4) * mm, "end": v(-688.03, 359.7) * mm});
            skLineSegment(sketch, "E320.MirrorCS", {"start": v(-681.68, 321.6) * mm, "end": v(-681.68, 308.9) * mm});
            skLineSegment(sketch, "E321.MirrorCS", {"start": v(-681.68, 321.6) * mm, "end": v(-681.68, 334.3) * mm});
            skLineSegment(sketch, "E322.MirrorCS", {"start": v(-681.68, 347) * mm, "end": v(-681.68, 359.7) * mm});
            skLineSegment(sketch, "E323.MirrorCS", {"start": v(-688.03, 347) * mm, "end": v(-688.03, 334.3) * mm});
            skLineSegment(sketch, "E324.MirrorCS", {"start": v(-688.03, 347) * mm, "end": v(-688.03, 359.7) * mm});
            skLineSegment(sketch, "E325.MirrorCS", {"start": v(-684.86, 385.1) * mm, "end": v(-684.86, 308.9) * mm});
            skLineSegment(sketch, "E326.MirrorCS", {"start": v(-681.68, 347) * mm, "end": v(-681.68, 334.3) * mm});
            skLineSegment(sketch, "E327.MirrorCS", {"start": v(-681.68, 372.4) * mm, "end": v(-681.68, 359.7) * mm});
            skLineSegment(sketch, "E328.MirrorCS", {"start": v(-681.68, 372.4) * mm, "end": v(-681.68, 385.1) * mm});
            skLineSegment(sketch, "E329.MirrorCS", {"start": v(-688.03, 321.6) * mm, "end": v(-688.03, 334.3) * mm});
            skSolve(sketch);
        }
        {
            var Q0;
            {var subQ15=sQuery(id+"F40.wireOp",EDGE,"E225.top");Q0=makeQuery(id+"F40.imprint","IMPRINT",FACE,{"disambiguationData":[TD([[makeQuery(id+"F40.imprint","IMPRINT",EDGE,{"derivedFrom":subQ15}),1.0]])]});}
            var Q1;
            {var subQ13=sQuery(id+"F40.wireOp",EDGE,"E229.top");Q1=makeQuery(id+"F40.imprint","IMPRINT",FACE,{"disambiguationData":[TD([[makeQuery(id+"F40.imprint","IMPRINT",EDGE,{"derivedFrom":subQ13}),1.0]])]});}
            var Q2;
            {var subQ5=sQuery(id+"F40.wireOp",EDGE,"E244.left");Q2=makeQuery(id+"F40.imprint","IMPRINT",FACE,{"disambiguationData":[TD([[makeQuery(id+"F40.imprint","IMPRINT",EDGE,{"derivedFrom":subQ5}),1.0]])]});}
            var Q3;
            {var subQ5=sQuery(id+"F40.wireOp",EDGE,"E244.right");Q3=makeQuery(id+"F40.imprint","IMPRINT",FACE,{"disambiguationData":[TD([[makeQuery(id+"F40.imprint","IMPRINT",EDGE,{"derivedFrom":subQ5}),-1.0]])]});}
            var Q4;
            {var subQ0=sQuery(id+"F40.wireOp",EDGE,"E256.MirrorCS");Q4=makeQuery(id+"F40.imprint","IMPRINT",FACE,{"disambiguationData":[TD([[makeQuery(id+"F40.imprint","IMPRINT",EDGE,{"derivedFrom":subQ0}),1.0]])]});}
            var Q5;
            {var subQ0=sQuery(id+"F40.wireOp",EDGE,"E251.MirrorCS");Q5=makeQuery(id+"F40.imprint","IMPRINT",FACE,{"disambiguationData":[TD([[makeQuery(id+"F40.imprint","IMPRINT",EDGE,{"derivedFrom":subQ0}),-1.0]])]});}
            var Q6;
            {var subQ0=sQuery(id+"F40.wireOp",EDGE,"E260.MirrorCS");var subQ1=sQuery(id+"F40.wireOp",EDGE,"E241.MirrorCS");var subQ2=makeQuery(id+"F40.imprint","INTERSECT",VERTEX,{"derivedFrom":[subQ1,subQ0]});Q6=makeQuery(id+"F40.imprint","IMPRINT",FACE,{"disambiguationData":[TD([[makeQuery(id+"F40.imprint","IMPRINT",EDGE,{"disambiguationData":[TD([[subQ2,-1.0]])],"derivedFrom":subQ1}),1.0]])]});}
            var Q7;
            {var subQ0=sQuery(id+"F40.wireOp",EDGE,"E265.MirrorCS");var subQ1=sQuery(id+"F40.wireOp",EDGE,"E233.top");var subQ2=makeQuery(id+"F40.imprint","INTERSECT",VERTEX,{"derivedFrom":[subQ1,subQ0]});Q7=makeQuery(id+"F40.imprint","IMPRINT",FACE,{"disambiguationData":[TD([[makeQuery(id+"F40.imprint","IMPRINT",EDGE,{"disambiguationData":[TD([[subQ2,-1.0]])],"derivedFrom":subQ1}),-1.0]])]});}
            var Q8;
            {var subQ48=sQuery(id+"F40.wireOp",EDGE,"E227.top");Q8=makeQuery(id+"F40.imprint","IMPRINT",FACE,{"disambiguationData":[TD([[makeQuery(id+"F40.imprint","IMPRINT",EDGE,{"derivedFrom":subQ48}),-1.0]])]});}
            var Q9;
            {var subQ22=sQuery(id+"F40.wireOp",EDGE,"E272.MirrorCS");Q9=makeQuery(id+"F40.imprint","IMPRINT",FACE,{"disambiguationData":[TD([[makeQuery(id+"F40.imprint","IMPRINT",EDGE,{"derivedFrom":subQ22}),1.0]])]});}
            var Q10;
            {var subQ3=sQuery(id+"F40.wireOp",EDGE,"E325.MirrorCS");var subQ5=sQuery(id+"F40.wireOp",EDGE,"E316.MirrorCS");var subQ6=makeQuery(id+"F40.imprint","INTERSECT",VERTEX,{"derivedFrom":[subQ5,subQ3]});Q10=makeQuery(id+"F40.imprint","IMPRINT",FACE,{"disambiguationData":[TD([[makeQuery(id+"F40.imprint","IMPRINT",EDGE,{"disambiguationData":[TD([[subQ6,-1.0]])],"derivedFrom":subQ5}),1.0]])]});}
            var Q11;
            {var subQ0=sQuery(id+"F40.wireOp",EDGE,"E319.MirrorCS");Q11=makeQuery(id+"F40.imprint","IMPRINT",FACE,{"disambiguationData":[TD([[makeQuery(id+"F40.imprint","IMPRINT",EDGE,{"derivedFrom":subQ0}),1.0]])]});}
            var Q12;
            {var subQ0=sQuery(id+"F40.wireOp",EDGE,"E327.MirrorCS");Q12=makeQuery(id+"F40.imprint","IMPRINT",FACE,{"disambiguationData":[TD([[makeQuery(id+"F40.imprint","IMPRINT",EDGE,{"derivedFrom":subQ0}),-1.0]])]});}
            var Q13;
            {var subQ0=sQuery(id+"F40.wireOp",EDGE,"E323.MirrorCS");Q13=makeQuery(id+"F40.imprint","IMPRINT",FACE,{"disambiguationData":[TD([[makeQuery(id+"F40.imprint","IMPRINT",EDGE,{"derivedFrom":subQ0}),1.0]])]});}
            var Q14;
            {var subQ0=sQuery(id+"F40.wireOp",EDGE,"E326.MirrorCS");Q14=makeQuery(id+"F40.imprint","IMPRINT",FACE,{"disambiguationData":[TD([[makeQuery(id+"F40.imprint","IMPRINT",EDGE,{"derivedFrom":subQ0}),-1.0]])]});}
            var Q15;
            {var subQ3=sQuery(id+"F40.wireOp",EDGE,"E325.MirrorCS");var subQ5=sQuery(id+"F40.wireOp",EDGE,"E318.MirrorCS");var subQ7=makeQuery(id+"F40.imprint","INTERSECT",VERTEX,{"derivedFrom":[subQ5,subQ3]});Q15=makeQuery(id+"F40.imprint","IMPRINT",FACE,{"disambiguationData":[TD([[makeQuery(id+"F40.imprint","IMPRINT",EDGE,{"disambiguationData":[TD([[subQ7,-1.0]])],"derivedFrom":subQ5}),-1.0]])]});}
            extrude(context, id + "F41", {"entities" : qUnion([Q0, Q1, Q2, Q3, Q4, Q5, Q6, Q7, Q8, Q9, Q10, Q11, Q12, Q13, Q14, Q15]), "depth" : 6.35 * mm});
        }
        {
            var Q0;
            Q0=makeQuery(id+"F3.opExtrude","CAP_FACE",FACE,{"disambiguationData":[OSD([sQuery(id+"F2.wireOp",EDGE,"E24.bottom"),sQuery(id+"F2.wireOp",EDGE,"E24.top"),sQuery(id+"F2.wireOp",EDGE,"E24.left"),sQuery(id+"F2.wireOp",EDGE,"E24.right"),sQuery(id+"F2.wireOp",EDGE,"E26.bottom"),sQuery(id+"F2.wireOp",EDGE,"E26.top"),sQuery(id+"F2.wireOp",EDGE,"E26.left"),sQuery(id+"F2.wireOp",EDGE,"E26.right"),sQuery(id+"F2.wireOp",EDGE,"E27.bottom"),sQuery(id+"F2.wireOp",EDGE,"E27.top"),sQuery(id+"F2.wireOp",EDGE,"E27.left"),sQuery(id+"F2.wireOp",EDGE,"E27.right"),sQuery(id+"F2.wireOp",EDGE,"E28.bottom"),sQuery(id+"F2.wireOp",EDGE,"E28.top"),sQuery(id+"F2.wireOp",EDGE,"E28.left"),sQuery(id+"F2.wireOp",EDGE,"E28.right"),sQuery(id+"F2.wireOp",EDGE,"E30.MirrorCS"),sQuery(id+"F2.wireOp",EDGE,"E31.MirrorCS"),sQuery(id+"F2.wireOp",EDGE,"E32.MirrorCS"),sQuery(id+"F2.wireOp",EDGE,"E33.MirrorCS"),sQuery(id+"F2.wireOp",EDGE,"E34.MirrorCS"),sQuery(id+"F2.wireOp",EDGE,"E35.MirrorCS"),sQuery(id+"F2.wireOp",EDGE,"E36.MirrorCS"),sQuery(id+"F2.wireOp",EDGE,"E37.MirrorCS")])],"isStart":true});
            var sketch = newSketch(context, id + "F42", { "sketchPlane" : qUnion([Q0])});
            skLineSegment(sketch, "E330.bottom", {"start": v(-350.78, 101.6) * mm, "end": v(-198.38, 101.6) * mm});
            skLineSegment(sketch, "E330.top", {"start": v(-350.78, 63.5) * mm, "end": v(-198.38, 63.5) * mm});
            skLineSegment(sketch, "E330.left", {"start": v(-350.78, 101.6) * mm, "end": v(-350.78, 63.5) * mm});
            skLineSegment(sketch, "E330.right", {"start": v(-198.38, 101.6) * mm, "end": v(-198.38, 63.5) * mm});
            skSolve(sketch);
        }
        {
            var Q0;
            Q0=makeQuery(id+"F42.imprint","IMPRINT",FACE,{"disambiguationData":[TD([[makeQuery(id+"F42.imprint","IMPRINT",EDGE,{"derivedFrom":sQuery(id+"F42.wireOp",EDGE,"E330.bottom")}),1.0]])]});
            extrude(context, id + "F43", {"entities" : qUnion([Q0]), "operationType" : NewBodyOperationType.REMOVE, "endBound" : BoundingType.UP_TO_NEXT, "oppositeDirection" : true, "depth" : 25.4 * mm});
        }
        {
            var Q0;
            Q0=makeQuery(id+"F1.opExtrude","CAP_FACE",FACE,{"disambiguationData":[OSD([sQuery(id+"F0.wireOp",EDGE,"E0.bottom"),sQuery(id+"F0.wireOp",EDGE,"E0.top"),sQuery(id+"F0.wireOp",EDGE,"E0.left"),sQuery(id+"F0.wireOp",EDGE,"E0.right"),sQuery(id+"F0.wireOp",EDGE,"E11.1.0.0"),sQuery(id+"F0.wireOp",EDGE,"E11.1.0.1"),sQuery(id+"F0.wireOp",EDGE,"E11.1.0.2"),sQuery(id+"F0.wireOp",EDGE,"E11.1.0.3"),sQuery(id+"F0.wireOp",EDGE,"E11.1.0.4"),sQuery(id+"F0.wireOp",EDGE,"E11.1.0.5"),sQuery(id+"F0.wireOp",EDGE,"E11.1.0.6"),sQuery(id+"F0.wireOp",EDGE,"E11.1.0.7"),sQuery(id+"F0.wireOp",EDGE,"E11.2.0.0"),sQuery(id+"F0.wireOp",EDGE,"E11.2.0.1"),sQuery(id+"F0.wireOp",EDGE,"E11.2.0.2"),sQuery(id+"F0.wireOp",EDGE,"E11.2.0.3"),sQuery(id+"F0.wireOp",EDGE,"E11.2.0.4"),sQuery(id+"F0.wireOp",EDGE,"E11.2.0.5"),sQuery(id+"F0.wireOp",EDGE,"E11.2.0.6"),sQuery(id+"F0.wireOp",EDGE,"E11.2.0.7"),sQuery(id+"F0.wireOp",EDGE,"E12.0.0.1"),sQuery(id+"F0.wireOp",EDGE,"E12.3.0.1"),sQuery(id+"F0.wireOp",EDGE,"E12.6.0.1"),sQuery(id+"F0.wireOp",EDGE,"E12.9.0.1"),sQuery(id+"F0.wireOp",EDGE,"E12.12.0.1"),sQuery(id+"F0.wireOp",EDGE,"E12.15.0.1"),sQuery(id+"F0.wireOp",EDGE,"E12.18.0.1"),sQuery(id+"F0.wireOp",EDGE,"E12.21.0.1"),sQuery(id+"F0.wireOp",EDGE,"E12.0.1.1"),sQuery(id+"F0.wireOp",EDGE,"E12.3.1.1"),sQuery(id+"F0.wireOp",EDGE,"E12.6.1.1"),sQuery(id+"F0.wireOp",EDGE,"E12.9.1.1"),sQuery(id+"F0.wireOp",EDGE,"E12.12.1.1"),sQuery(id+"F0.wireOp",EDGE,"E12.15.1.1"),sQuery(id+"F0.wireOp",EDGE,"E12.18.1.1"),sQuery(id+"F0.wireOp",EDGE,"E12.21.1.1"),sQuery(id+"F0.wireOp",EDGE,"E3"),sQuery(id+"F0.wireOp",EDGE,"E6.MirrorCS"),sQuery(id+"F0.wireOp",EDGE,"E5.MirrorCS"),sQuery(id+"F0.wireOp",EDGE,"E10.MirrorCS"),sQuery(id+"F0.wireOp",EDGE,"E9.MirrorCS"),sQuery(id+"F0.wireOp",EDGE,"E8.MirrorCS"),sQuery(id+"F0.wireOp",EDGE,"E7.MirrorCS"),sQuery(id+"F0.wireOp",EDGE,"E4"),sQuery(id+"F0.wireOp",EDGE,"E13.bottom"),sQuery(id+"F0.wireOp",EDGE,"E13.top"),sQuery(id+"F0.wireOp",EDGE,"E13.left"),sQuery(id+"F0.wireOp",EDGE,"E13.right"),sQuery(id+"F0.wireOp",EDGE,"E14.0.1.0"),sQuery(id+"F0.wireOp",EDGE,"E14.0.1.1"),sQuery(id+"F0.wireOp",EDGE,"E14.0.1.2"),sQuery(id+"F0.wireOp",EDGE,"E14.0.1.3"),sQuery(id+"F0.wireOp",EDGE,"E15.MirrorCS"),sQuery(id+"F0.wireOp",EDGE,"E16.MirrorCS"),sQuery(id+"F0.wireOp",EDGE,"E17.MirrorCS"),sQuery(id+"F0.wireOp",EDGE,"E18.MirrorCS"),sQuery(id+"F0.wireOp",EDGE,"E19.MirrorCS"),sQuery(id+"F0.wireOp",EDGE,"E20.MirrorCS"),sQuery(id+"F0.wireOp",EDGE,"E21.MirrorCS"),sQuery(id+"F0.wireOp",EDGE,"E23")])],"isStart":true});
            var sketch = newSketch(context, id + "F44", { "sketchPlane" : qUnion([Q0])});
            skLineSegment(sketch, "E331.bottom", {"start": v(-152.4, 101.6) * mm, "end": v(0, 101.6) * mm});
            skLineSegment(sketch, "E331.top", {"start": v(-152.4, 63.5) * mm, "end": v(0, 63.5) * mm});
            skLineSegment(sketch, "E331.left", {"start": v(-152.4, 101.6) * mm, "end": v(-152.4, 63.5) * mm});
            skLineSegment(sketch, "E331.right", {"start": v(0, 101.6) * mm, "end": v(0, 63.5) * mm});
            skSolve(sketch);
        }
        {
            var Q0;
            Q0=makeQuery(id+"F44.imprint","IMPRINT",FACE,{"disambiguationData":[TD([[makeQuery(id+"F44.imprint","IMPRINT",EDGE,{"derivedFrom":sQuery(id+"F44.wireOp",EDGE,"E331.bottom")}),1.0]])]});
            extrude(context, id + "F45", {"entities" : qUnion([Q0]), "operationType" : NewBodyOperationType.REMOVE, "endBound" : BoundingType.UP_TO_NEXT, "oppositeDirection" : true, "depth" : 25.4 * mm});
        }
        {
            var Q0;
            Q0=makeQuery(id+"F3.opExtrude","CAP_FACE",FACE,{"disambiguationData":[OSD([sQuery(id+"F2.wireOp",EDGE,"E24.bottom"),sQuery(id+"F2.wireOp",EDGE,"E24.top"),sQuery(id+"F2.wireOp",EDGE,"E24.left"),sQuery(id+"F2.wireOp",EDGE,"E24.right"),sQuery(id+"F2.wireOp",EDGE,"E26.bottom"),sQuery(id+"F2.wireOp",EDGE,"E26.top"),sQuery(id+"F2.wireOp",EDGE,"E26.left"),sQuery(id+"F2.wireOp",EDGE,"E26.right"),sQuery(id+"F2.wireOp",EDGE,"E27.bottom"),sQuery(id+"F2.wireOp",EDGE,"E27.top"),sQuery(id+"F2.wireOp",EDGE,"E27.left"),sQuery(id+"F2.wireOp",EDGE,"E27.right"),sQuery(id+"F2.wireOp",EDGE,"E28.bottom"),sQuery(id+"F2.wireOp",EDGE,"E28.top"),sQuery(id+"F2.wireOp",EDGE,"E28.left"),sQuery(id+"F2.wireOp",EDGE,"E28.right"),sQuery(id+"F2.wireOp",EDGE,"E30.MirrorCS"),sQuery(id+"F2.wireOp",EDGE,"E31.MirrorCS"),sQuery(id+"F2.wireOp",EDGE,"E32.MirrorCS"),sQuery(id+"F2.wireOp",EDGE,"E33.MirrorCS"),sQuery(id+"F2.wireOp",EDGE,"E34.MirrorCS"),sQuery(id+"F2.wireOp",EDGE,"E35.MirrorCS"),sQuery(id+"F2.wireOp",EDGE,"E36.MirrorCS"),sQuery(id+"F2.wireOp",EDGE,"E37.MirrorCS")])],"isStart":true});
            var sketch = newSketch(context, id + "F46", { "sketchPlane" : qUnion([Q0])});
            skLineSegment(sketch, "E332", {"start": v(-350.78, 63.5) * mm, "end": v(-376.18, 0) * mm});
            skLineSegment(sketch, "E333", {"start": v(-376.18, 0) * mm, "end": v(-350.78, 0) * mm});
            skLineSegment(sketch, "E334", {"start": v(-198.38, 63.5) * mm, "end": v(-172.98, 0) * mm});
            skLineSegment(sketch, "E335", {"start": v(-172.98, 0) * mm, "end": v(-198.38, 0) * mm});
            skLineSegment(sketch, "E336", {"start": v(-198.38, 0) * mm, "end": v(-198.38, 63.5) * mm});
            skLineSegment(sketch, "E337", {"start": v(-350.78, 63.5) * mm, "end": v(-350.78, 0) * mm});
            skSolve(sketch);
        }
        {
            var Q0;
            Q0=makeQuery(id+"F46.imprint","IMPRINT",FACE,{"disambiguationData":[TD([[makeQuery(id+"F46.imprint","IMPRINT",EDGE,{"derivedFrom":sQuery(id+"F46.wireOp",EDGE,"E332")}),1.0]])]});
            var Q1;
            Q1=makeQuery(id+"F46.imprint","IMPRINT",FACE,{"disambiguationData":[TD([[makeQuery(id+"F46.imprint","IMPRINT",EDGE,{"derivedFrom":sQuery(id+"F46.wireOp",EDGE,"E334")}),-1.0]])]});
            extrude(context, id + "F47", {"entities" : qUnion([Q0, Q1]), "operationType" : NewBodyOperationType.ADD, "oppositeDirection" : true, "depth" : 6.35 * mm});
        }
        {
            var Q0;
            {var subQ0=sQuery(id+"F42.wireOp",EDGE,"E330.top");Q0=makeQuery(id+"F47.boolean.opBoolean","MERGE",EDGE,{"derivedFrom":[makeQuery(id+"F43.boolean.opBoolean","COPY",EDGE,{"derivedFrom":makeQuery(id+"F43.opExtrude","SWEPT_EDGE",EDGE,{"disambiguationData":[OSD([sQuery(id+"F2.wireOp",EDGE,"E24.right"),subQ0,sQuery(id+"F42.wireOp",EDGE,"E330.left")])]})}),makeQuery(id+"F47.opExtrude","SWEPT_EDGE",EDGE,{"disambiguationData":[OSD([subQ0,sQuery(id+"F46.wireOp",EDGE,"E332"),sQuery(id+"F46.wireOp",EDGE,"E337")])]})]});}
            var Q1;
            {var subQ0=sQuery(id+"F42.wireOp",EDGE,"E330.top");Q1=makeQuery(id+"F47.boolean.opBoolean","MERGE",EDGE,{"derivedFrom":[makeQuery(id+"F43.boolean.opBoolean","COPY",EDGE,{"derivedFrom":makeQuery(id+"F43.opExtrude","SWEPT_EDGE",EDGE,{"disambiguationData":[OSD([sQuery(id+"F2.wireOp",EDGE,"E24.left"),subQ0,sQuery(id+"F42.wireOp",EDGE,"E330.right")])]})}),makeQuery(id+"F47.opExtrude","SWEPT_EDGE",EDGE,{"disambiguationData":[OSD([subQ0,sQuery(id+"F46.wireOp",EDGE,"E334"),sQuery(id+"F46.wireOp",EDGE,"E336")])]})]});}
            var Q2;
            Q2=makeQuery(id+"F47.opExtrude","SWEPT_EDGE",EDGE,{"disambiguationData":[OSD([sQuery(id+"F46.wireOp",EDGE,"E332"),sQuery(id+"F46.wireOp",EDGE,"E333")])]});
            var Q3;
            Q3=makeQuery(id+"F47.opExtrude","SWEPT_EDGE",EDGE,{"disambiguationData":[OSD([sQuery(id+"F46.wireOp",EDGE,"E334"),sQuery(id+"F46.wireOp",EDGE,"E335")])]});
            fillet(context, id + "F48", {"entities" : qUnion([Q0, Q1, Q2, Q3]), "radius" : 5.08 * mm, "tangentPropagation" : true, "allowEdgeOverflow" : false});
        }
        {
            var Q0;
            Q0=makeQuery(id+"F1.opExtrude","CAP_FACE",FACE,{"disambiguationData":[OSD([sQuery(id+"F0.wireOp",EDGE,"E0.bottom"),sQuery(id+"F0.wireOp",EDGE,"E0.top"),sQuery(id+"F0.wireOp",EDGE,"E0.left"),sQuery(id+"F0.wireOp",EDGE,"E0.right"),sQuery(id+"F0.wireOp",EDGE,"E11.1.0.0"),sQuery(id+"F0.wireOp",EDGE,"E11.1.0.1"),sQuery(id+"F0.wireOp",EDGE,"E11.1.0.2"),sQuery(id+"F0.wireOp",EDGE,"E11.1.0.3"),sQuery(id+"F0.wireOp",EDGE,"E11.1.0.4"),sQuery(id+"F0.wireOp",EDGE,"E11.1.0.5"),sQuery(id+"F0.wireOp",EDGE,"E11.1.0.6"),sQuery(id+"F0.wireOp",EDGE,"E11.1.0.7"),sQuery(id+"F0.wireOp",EDGE,"E11.2.0.0"),sQuery(id+"F0.wireOp",EDGE,"E11.2.0.1"),sQuery(id+"F0.wireOp",EDGE,"E11.2.0.2"),sQuery(id+"F0.wireOp",EDGE,"E11.2.0.3"),sQuery(id+"F0.wireOp",EDGE,"E11.2.0.4"),sQuery(id+"F0.wireOp",EDGE,"E11.2.0.5"),sQuery(id+"F0.wireOp",EDGE,"E11.2.0.6"),sQuery(id+"F0.wireOp",EDGE,"E11.2.0.7"),sQuery(id+"F0.wireOp",EDGE,"E12.0.0.1"),sQuery(id+"F0.wireOp",EDGE,"E12.3.0.1"),sQuery(id+"F0.wireOp",EDGE,"E12.6.0.1"),sQuery(id+"F0.wireOp",EDGE,"E12.9.0.1"),sQuery(id+"F0.wireOp",EDGE,"E12.12.0.1"),sQuery(id+"F0.wireOp",EDGE,"E12.15.0.1"),sQuery(id+"F0.wireOp",EDGE,"E12.18.0.1"),sQuery(id+"F0.wireOp",EDGE,"E12.21.0.1"),sQuery(id+"F0.wireOp",EDGE,"E12.0.1.1"),sQuery(id+"F0.wireOp",EDGE,"E12.3.1.1"),sQuery(id+"F0.wireOp",EDGE,"E12.6.1.1"),sQuery(id+"F0.wireOp",EDGE,"E12.9.1.1"),sQuery(id+"F0.wireOp",EDGE,"E12.12.1.1"),sQuery(id+"F0.wireOp",EDGE,"E12.15.1.1"),sQuery(id+"F0.wireOp",EDGE,"E12.18.1.1"),sQuery(id+"F0.wireOp",EDGE,"E12.21.1.1"),sQuery(id+"F0.wireOp",EDGE,"E3"),sQuery(id+"F0.wireOp",EDGE,"E6.MirrorCS"),sQuery(id+"F0.wireOp",EDGE,"E5.MirrorCS"),sQuery(id+"F0.wireOp",EDGE,"E10.MirrorCS"),sQuery(id+"F0.wireOp",EDGE,"E9.MirrorCS"),sQuery(id+"F0.wireOp",EDGE,"E8.MirrorCS"),sQuery(id+"F0.wireOp",EDGE,"E7.MirrorCS"),sQuery(id+"F0.wireOp",EDGE,"E4"),sQuery(id+"F0.wireOp",EDGE,"E13.bottom"),sQuery(id+"F0.wireOp",EDGE,"E13.top"),sQuery(id+"F0.wireOp",EDGE,"E13.left"),sQuery(id+"F0.wireOp",EDGE,"E13.right"),sQuery(id+"F0.wireOp",EDGE,"E14.0.1.0"),sQuery(id+"F0.wireOp",EDGE,"E14.0.1.1"),sQuery(id+"F0.wireOp",EDGE,"E14.0.1.2"),sQuery(id+"F0.wireOp",EDGE,"E14.0.1.3"),sQuery(id+"F0.wireOp",EDGE,"E15.MirrorCS"),sQuery(id+"F0.wireOp",EDGE,"E16.MirrorCS"),sQuery(id+"F0.wireOp",EDGE,"E17.MirrorCS"),sQuery(id+"F0.wireOp",EDGE,"E18.MirrorCS"),sQuery(id+"F0.wireOp",EDGE,"E19.MirrorCS"),sQuery(id+"F0.wireOp",EDGE,"E20.MirrorCS"),sQuery(id+"F0.wireOp",EDGE,"E21.MirrorCS"),sQuery(id+"F0.wireOp",EDGE,"E23")])],"isStart":true});
            var sketch = newSketch(context, id + "F49", { "sketchPlane" : qUnion([Q0])});
            skLineSegment(sketch, "E338", {"start": v(-152.4, 63.5) * mm, "end": v(-177.8, 0) * mm});
            skLineSegment(sketch, "E339", {"start": v(-177.8, 0) * mm, "end": v(-152.4, 0) * mm});
            skLineSegment(sketch, "E340", {"start": v(-152.4, 0) * mm, "end": v(-152.4, 63.5) * mm});
            skLineSegment(sketch, "E341", {"start": v(0, 63.5) * mm, "end": v(0, 0) * mm});
            skLineSegment(sketch, "E342", {"start": v(0, 0) * mm, "end": v(25.4, 0) * mm});
            skLineSegment(sketch, "E343", {"start": v(25.4, 0) * mm, "end": v(0, 63.5) * mm});
            skSolve(sketch);
        }
        {
            var Q0;
            Q0=makeQuery(id+"F49.imprint","IMPRINT",FACE,{"disambiguationData":[TD([[makeQuery(id+"F49.imprint","IMPRINT",EDGE,{"derivedFrom":sQuery(id+"F49.wireOp",EDGE,"E338")}),1.0]])]});
            var Q1;
            Q1=makeQuery(id+"F49.imprint","IMPRINT",FACE,{"disambiguationData":[TD([[makeQuery(id+"F49.imprint","IMPRINT",EDGE,{"derivedFrom":sQuery(id+"F49.wireOp",EDGE,"E341")}),-1.0]])]});
            extrude(context, id + "F50", {"entities" : qUnion([Q0, Q1]), "operationType" : NewBodyOperationType.ADD, "oppositeDirection" : true, "depth" : 6.35 * mm});
        }
        {
            var Q0;
            {var subQ0=sQuery(id+"F44.wireOp",EDGE,"E331.top");Q0=makeQuery(id+"F50.boolean.opBoolean","MERGE",EDGE,{"derivedFrom":[makeQuery(id+"F45.boolean.opBoolean","COPY",EDGE,{"derivedFrom":makeQuery(id+"F45.opExtrude","SWEPT_EDGE",EDGE,{"disambiguationData":[OSD([sQuery(id+"F0.wireOp",EDGE,"E0.right"),subQ0,sQuery(id+"F44.wireOp",EDGE,"E331.left")])]})}),makeQuery(id+"F50.opExtrude","SWEPT_EDGE",EDGE,{"disambiguationData":[OSD([subQ0,sQuery(id+"F49.wireOp",EDGE,"E338"),sQuery(id+"F49.wireOp",EDGE,"E340")])]})]});}
            var Q1;
            {var subQ0=sQuery(id+"F44.wireOp",EDGE,"E331.top");Q1=makeQuery(id+"F50.boolean.opBoolean","MERGE",EDGE,{"derivedFrom":[makeQuery(id+"F45.boolean.opBoolean","COPY",EDGE,{"derivedFrom":makeQuery(id+"F45.opExtrude","SWEPT_EDGE",EDGE,{"disambiguationData":[OSD([sQuery(id+"F0.wireOp",EDGE,"E0.left"),subQ0,sQuery(id+"F44.wireOp",EDGE,"E331.right")])]})}),makeQuery(id+"F50.opExtrude","SWEPT_EDGE",EDGE,{"disambiguationData":[OSD([subQ0,sQuery(id+"F49.wireOp",EDGE,"E341"),sQuery(id+"F49.wireOp",EDGE,"E343")])]})]});}
            var Q2;
            Q2=makeQuery(id+"F50.opExtrude","SWEPT_EDGE",EDGE,{"disambiguationData":[OSD([sQuery(id+"F49.wireOp",EDGE,"E342"),sQuery(id+"F49.wireOp",EDGE,"E343")])]});
            var Q3;
            Q3=makeQuery(id+"F50.opExtrude","SWEPT_EDGE",EDGE,{"disambiguationData":[OSD([sQuery(id+"F49.wireOp",EDGE,"E338"),sQuery(id+"F49.wireOp",EDGE,"E339")])]});
            fillet(context, id + "F51", {"entities" : qUnion([Q0, Q1, Q2, Q3]), "radius" : 5.08 * mm, "tangentPropagation" : true, "allowEdgeOverflow" : false});
        }
        {
            var Q0;
            Q0=qCreatedBy(makeId("Right.planeOp"),FACE);
            var sketch = newSketch(context, id + "F52", { "sketchPlane" : qUnion([Q0])});
            skCircle(sketch, "E344", {"center": v(-40.92, 0) * mm, "radius": 12.7 * mm});
            skCircle(sketch, "E345", {"center": v(-40.92, 7.3) * mm, "radius": 1.52 * mm});
            skLineSegment(sketch, "E346", {"start": v(-40.92, 0) * mm, "end": v(-40.92, 7.3) * mm, "construction": true});
            skLineSegment(sketch, "E347", {"start": v(-40.92, 7.3) * mm, "end": v(-40.92, 0) * mm, "construction": true});
            skCircle(sketch, "E348.MirrorC", {"center": v(-40.92, -7.3) * mm, "radius": 1.52 * mm});
            skCircle(sketch, "E349", {"center": v(-40.92, 0) * mm, "radius": 4.45 * mm});
            skSolve(sketch);
        }
        {
            var Q0;
            Q0=makeQuery(id+"F52.imprint","IMPRINT",FACE,{"disambiguationData":[TD([[makeQuery(id+"F52.imprint","IMPRINT",EDGE,{"derivedFrom":sQuery(id+"F52.wireOp",EDGE,"E344")}),1.0]])]});
            extrude(context, id + "F53", {"entities" : qUnion([Q0]), "depth" : 6.35 * mm});
        }
    });
